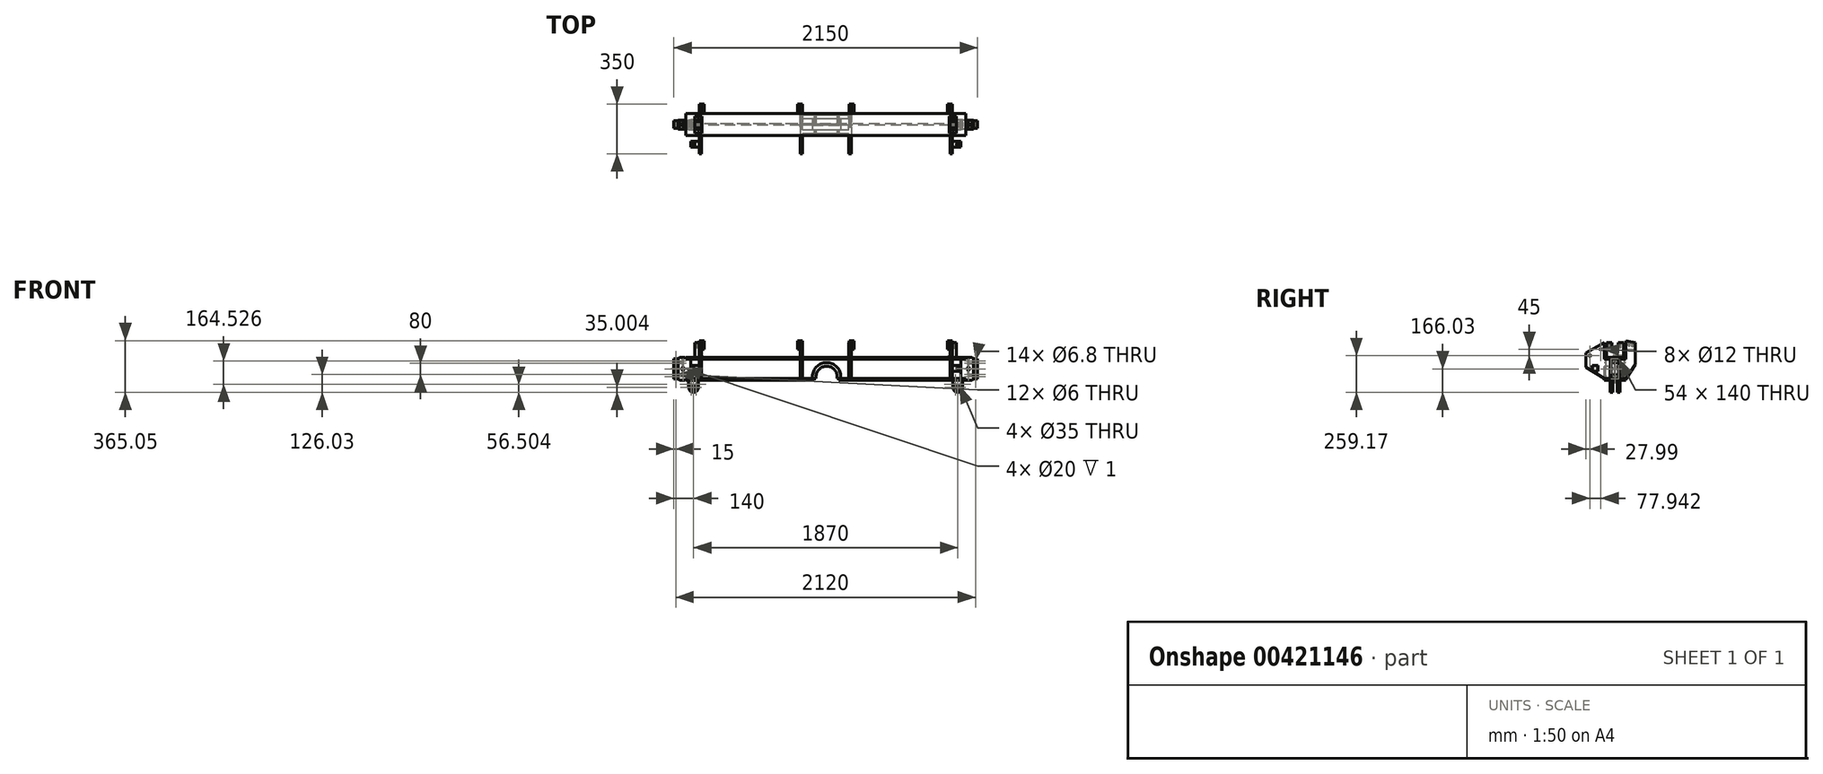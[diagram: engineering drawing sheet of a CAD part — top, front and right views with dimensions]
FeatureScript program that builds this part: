
annotation { "Feature Type Name" : "Feature", "Feature Type Description" : "" }
export const myFeature = defineFeature(function(context is Context, id is Id, definition is map)
    precondition{}
    {
        {
            var Q0;
            Q0=qCreatedBy(makeId("Right.planeOp"),FACE);
            var sketch = newSketch(context, id + "F0", { "sketchPlane" : qUnion([Q0])});
            skLineSegment(sketch, "E0.bottom", {"start": v(-77.22, 81.03) * mm, "end": v(77.22, 81.03) * mm});
            skLineSegment(sketch, "E0.top", {"start": v(-77.22, -81.03) * mm, "end": v(77.22, -81.03) * mm});
            skLineSegment(sketch, "E0.left", {"start": v(-77.22, 81.03) * mm, "end": v(-77.22, 69.47) * mm});
            skLineSegment(sketch, "E0.right", {"start": v(77.22, 81.03) * mm, "end": v(77.22, 69.47) * mm});
            skPoint(sketch, "E0.middle", {"position": v(0, 0) * mm});
            skLineSegment(sketch, "E1", {"start": v(0, 87.3) * mm, "end": v(0, -92.44) * mm, "construction": true});
            skLineSegment(sketch, "E2.0", {"start": v(-77.22, 69.47) * mm, "end": v(-16.76, 69.47) * mm});
            skLineSegment(sketch, "E3.0", {"start": v(-77.22, -69.47) * mm, "end": v(-16.76, -69.47) * mm});
            skLineSegment(sketch, "E4.0", {"start": v(-4.06, 56.77) * mm, "end": v(-4.06, -56.77) * mm});
            skLineSegment(sketch, "E5.0", {"start": v(4.06, 56.77) * mm, "end": v(4.06, -56.77) * mm});
            skLineSegment(sketch, "E6.trimOffspring", {"start": v(16.76, -69.47) * mm, "end": v(77.22, -69.47) * mm});
            skLineSegment(sketch, "E7.trimOffspring", {"start": v(16.76, 69.47) * mm, "end": v(77.22, 69.47) * mm});
            skLineSegment(sketch, "E8.trimOffspring", {"start": v(-77.22, -69.47) * mm, "end": v(-77.22, -81.03) * mm});
            skLineSegment(sketch, "E9.trimOffspring", {"start": v(77.22, -69.47) * mm, "end": v(77.22, -81.03) * mm});
            skPoint(sketch, "E10.visualSharp", {"position": v(-4.06, 69.47) * mm});
            skArc(sketch, "E10.filletArc", {"start": v(-4.06, 56.77) * mm, "mid": v(-7.78, 65.75) * mm, "end": v(-16.76, 69.47) * mm});
            skPoint(sketch, "E11.visualSharp", {"position": v(4.06, 69.47) * mm});
            skArc(sketch, "E11.filletArc", {"start": v(16.76, 69.47) * mm, "mid": v(7.78, 65.75) * mm, "end": v(4.06, 56.77) * mm});
            skPoint(sketch, "E12.visualSharp", {"position": v(4.06, -69.47) * mm});
            skArc(sketch, "E12.filletArc", {"start": v(4.06, -56.77) * mm, "mid": v(7.78, -65.75) * mm, "end": v(16.76, -69.47) * mm});
            skPoint(sketch, "E13.visualSharp", {"position": v(-4.06, -69.47) * mm});
            skArc(sketch, "E13.filletArc", {"start": v(-16.76, -69.47) * mm, "mid": v(-7.78, -65.75) * mm, "end": v(-4.06, -56.77) * mm});
            skSolve(sketch);
        }
        {
            var Q0;
            Q0=qSketchRegion(id+"F0",true);
            extrude(context, id + "F1", {"entities" : qUnion([Q0]), "endBound" : BoundingType.SYMMETRIC, "depth" : 1980 * mm});
        }
        {
            var Q0;
            Q0=makeQuery(id+"F1.opExtrude","SWEPT_FACE",FACE,{"disambiguationData":[OSD([sQuery(id+"F0.wireOp",EDGE,"E4.0")])]});
            var sketch = newSketch(context, id + "F2", { "sketchPlane" : qUnion([Q0])});
            skLineSegment(sketch, "E14", {"start": v(0, 173.84) * mm, "end": v(0, -192.2) * mm, "construction": true});
            skLineSegment(sketch, "E15.0", {"start": v(-990, 69.47) * mm, "end": v(-990, -69.47) * mm, "construction": true});
            skLineSegment(sketch, "E16.0", {"start": v(990, 69.47) * mm, "end": v(-990, 69.47) * mm, "construction": true});
            skLineSegment(sketch, "E17.0", {"start": v(990, -69.47) * mm, "end": v(-990, -69.47) * mm, "construction": true});
            skPoint(sketch, "E18.orphan", {"position": v(-990, 56.77) * mm});
            skPoint(sketch, "E19.orphan", {"position": v(-990, -56.77) * mm});
            skLineSegment(sketch, "E20.bottom", {"start": v(-990, 69.47) * mm, "end": v(-955, 69.47) * mm});
            skLineSegment(sketch, "E20.top", {"start": v(-990, -69.47) * mm, "end": v(-955, -69.47) * mm});
            skLineSegment(sketch, "E20.left", {"start": v(-990, 69.47) * mm, "end": v(-990, -69.47) * mm});
            skLineSegment(sketch, "E20.right", {"start": v(-955, 69.47) * mm, "end": v(-955, -69.47) * mm});
            skLineSegment(sketch, "E21.MirrorCS", {"start": v(990, -69.47) * mm, "end": v(955, -69.47) * mm});
            skLineSegment(sketch, "E22.MirrorCS", {"start": v(990, 69.47) * mm, "end": v(955, 69.47) * mm});
            skLineSegment(sketch, "E23.MirrorCS", {"start": v(990, 69.47) * mm, "end": v(990, -69.47) * mm});
            skLineSegment(sketch, "E24.MirrorCS", {"start": v(955, 69.47) * mm, "end": v(955, -69.47) * mm});
            skPoint(sketch, "E25.MirrorP", {"position": v(990, -56.77) * mm});
            skPoint(sketch, "E26.MirrorP", {"position": v(990, 56.77) * mm});
            skLineSegment(sketch, "E27.MirrorCS", {"start": v(990, 69.47) * mm, "end": v(990, -69.47) * mm, "construction": true});
            skSolve(sketch);
        }
        {
            var Q0;
            Q0=qSketchRegion(id+"F2",true);
            extrude(context, id + "F3", {"entities" : qUnion([Q0]), "operationType" : NewBodyOperationType.REMOVE, "endBound" : BoundingType.SYMMETRIC, "oppositeDirection" : true, "depth" : 50 * mm});
        }
        {
            var Q0;
            Q0=qCreatedBy(makeId("Front.planeOp"),FACE);
            var sketch = newSketch(context, id + "F4", { "sketchPlane" : qUnion([Q0])});
            skLineSegment(sketch, "E28", {"start": v(0, 276.7) * mm, "end": v(0, -349.05) * mm, "construction": true});
            skLineSegment(sketch, "E29.0", {"start": v(-1075, 276.7) * mm, "end": v(-1075, -349.05) * mm, "construction": true});
            skLineSegment(sketch, "E30.0", {"start": v(990, 81.03) * mm, "end": v(-1045, 81.03) * mm, "construction": true});
            skLineSegment(sketch, "E31.0", {"start": v(990, -81.03) * mm, "end": v(-1045, -81.03) * mm, "construction": true});
            skLineSegment(sketch, "E32.0", {"start": v(-955, -69.47) * mm, "end": v(-955, 69.47) * mm, "construction": true});
            skLineSegment(sketch, "E33.0", {"start": v(990, -69.47) * mm, "end": v(-990, -69.47) * mm, "construction": true});
            skLineSegment(sketch, "E34.0", {"start": v(990, 69.47) * mm, "end": v(-990, 69.47) * mm, "construction": true});
            skPoint(sketch, "E35.orphan", {"position": v(-955, 56.77) * mm});
            skPoint(sketch, "E36.orphan", {"position": v(-955, -56.77) * mm});
            skPoint(sketch, "E37.orphan", {"position": v(-990, 81.03) * mm});
            skPoint(sketch, "E38.orphan", {"position": v(-990, -81.03) * mm});
            skLineSegment(sketch, "E39", {"start": v(-990, 81.03) * mm, "end": v(-990, 69.47) * mm, "construction": true});
            skLineSegment(sketch, "E40.0", {"start": v(-1045, 81.03) * mm, "end": v(-1045, 70) * mm, "construction": true});
            skLineSegment(sketch, "E41", {"start": v(0, 0) * mm, "end": v(-1199.42, 0) * mm, "construction": true});
            skLineSegment(sketch, "E42.0", {"start": v(0, 70) * mm, "end": v(-990, 70) * mm, "construction": true});
            skLineSegment(sketch, "E43.trimOffspring", {"start": v(-1045, 70) * mm, "end": v(-1075, 70) * mm, "construction": true});
            skLineSegment(sketch, "E44.MirrorCS", {"start": v(-1045, -70) * mm, "end": v(-1075, -70) * mm, "construction": true});
            skPoint(sketch, "E45.orphan", {"position": v(-1199.42, 70) * mm});
            skPoint(sketch, "E46.orphan", {"position": v(-1199.42, -70) * mm});
            skLineSegment(sketch, "E47.trimOffspring", {"start": v(-1045, -70) * mm, "end": v(-1045, -81.03) * mm, "construction": true});
            skLineSegment(sketch, "E48.trimOffspring", {"start": v(-990, -69.47) * mm, "end": v(-990, -81.03) * mm, "construction": true});
            skLineSegment(sketch, "E49.bottom", {"start": v(-1075, 70) * mm, "end": v(-1045, 70) * mm});
            skLineSegment(sketch, "E49.top", {"start": v(-1075, -70) * mm, "end": v(-1045, -70) * mm});
            skLineSegment(sketch, "E49.left", {"start": v(-1075, 70) * mm, "end": v(-1075, -70) * mm});
            skLineSegment(sketch, "E50.bottom", {"start": v(-1045, 81.03) * mm, "end": v(-990, 81.03) * mm});
            skLineSegment(sketch, "E50.top", {"start": v(-1045, -81.03) * mm, "end": v(-990, -81.03) * mm});
            skLineSegment(sketch, "E50.left", {"start": v(-1045, 81.03) * mm, "end": v(-1045, 70) * mm});
            skLineSegment(sketch, "E50.right", {"start": v(-990, 81.03) * mm, "end": v(-990, 69.47) * mm});
            skLineSegment(sketch, "E51.bottom", {"start": v(-990, 70) * mm, "end": v(-955, 70) * mm});
            skLineSegment(sketch, "E51.top", {"start": v(-990, -69.47) * mm, "end": v(-955, -69.47) * mm});
            skLineSegment(sketch, "E51.left", {"start": v(-990, 70) * mm, "end": v(-990, 69.47) * mm});
            skLineSegment(sketch, "E51.right", {"start": v(-955, 70) * mm, "end": v(-955, -69.47) * mm});
            skLineSegment(sketch, "E52.trimOffspring", {"start": v(-990, -69.47) * mm, "end": v(-990, -81.03) * mm});
            skLineSegment(sketch, "E53.trimOffspring", {"start": v(-1045, -70) * mm, "end": v(-1045, -81.03) * mm});
            skSolve(sketch);
        }
        {
            var Q0;
            Q0=qSketchRegion(id+"F4",true);
            extrude(context, id + "F5", {"entities" : qUnion([Q0]), "endBound" : BoundingType.SYMMETRIC, "depth" : 63.5 * mm});
        }
        {
            var Q0;
            Q0=makeQuery(id+"F5.opExtrude","SWEPT_FACE",FACE,{"disambiguationData":[OSD([sQuery(id+"F4.wireOp",EDGE,"E49.bottom")])]});
            var sketch = newSketch(context, id + "F6", { "sketchPlane" : qUnion([Q0])});
            skLineSegment(sketch, "E54", {"start": v(-948.4, 0) * mm, "end": v(-1101.52, 0) * mm, "construction": true});
            skLineSegment(sketch, "E55.0", {"start": v(-1045, -31.75) * mm, "end": v(-1045, 31.75) * mm, "construction": true});
            skLineSegment(sketch, "E56.0", {"start": v(-948.4, 27) * mm, "end": v(-1101.52, 27) * mm, "construction": true});
            skLineSegment(sketch, "E57.bottom", {"start": v(-1075, 31.75) * mm, "end": v(-1045, 31.75) * mm});
            skLineSegment(sketch, "E57.top", {"start": v(-1075, 27) * mm, "end": v(-1045, 27) * mm});
            skLineSegment(sketch, "E57.left", {"start": v(-1075, 31.75) * mm, "end": v(-1075, 27) * mm});
            skLineSegment(sketch, "E57.right", {"start": v(-1045, 31.75) * mm, "end": v(-1045, 27) * mm});
            skLineSegment(sketch, "E58.MirrorCS", {"start": v(-1045, -31.75) * mm, "end": v(-1045, -27) * mm});
            skLineSegment(sketch, "E59.MirrorCS", {"start": v(-1075, -31.75) * mm, "end": v(-1075, -27) * mm});
            skLineSegment(sketch, "E60.MirrorCS", {"start": v(-1075, -27) * mm, "end": v(-1045, -27) * mm});
            skLineSegment(sketch, "E61.MirrorCS", {"start": v(-1075, -31.75) * mm, "end": v(-1045, -31.75) * mm});
            skSolve(sketch);
        }
        {
            var Q0;
            Q0=qSketchRegion(id+"F6",true);
            extrude(context, id + "F7", {"entities" : qUnion([Q0]), "operationType" : NewBodyOperationType.REMOVE, "endBound" : BoundingType.THROUGH_ALL, "oppositeDirection" : true, "depth" : 25 * mm});
        }
        {
            var Q0;
            Q0=makeQuery(id+"F5.opExtrude","SWEPT_FACE",FACE,{"disambiguationData":[OSD([sQuery(id+"F4.wireOp",EDGE,"E50.bottom")])]});
            var sketch = newSketch(context, id + "F8", { "sketchPlane" : qUnion([Q0])});
            skLineSegment(sketch, "E62.0", {"start": v(-1075, -27) * mm, "end": v(-1075, 27) * mm, "construction": true});
            skLineSegment(sketch, "E63", {"start": v(-919.6, 0) * mm, "end": v(-1088.25, 0) * mm, "construction": true});
            skPoint(sketch, "E63.endSnap0", {"position": v(-1075, 0) * mm});
            skLineSegment(sketch, "E64.0", {"start": v(-1010, -27) * mm, "end": v(-1010, 27) * mm, "construction": true});
            skPoint(sketch, "E65", {"position": v(-1010, 0) * mm});
            skSolve(sketch);
        }
        {
            var Q0;
            Q0=sQuery(id+"F8.wireOp",VERTEX,"E65");
            var Q1;
            Q1=makeQuery(id+"F5.opExtrude","SWEPT_BODY",BODY,{"disambiguationData":[OSD([sQuery(id+"F4.wireOp",EDGE,"E49.bottom"),sQuery(id+"F4.wireOp",EDGE,"E49.top"),sQuery(id+"F4.wireOp",EDGE,"E49.left"),sQuery(id+"F4.wireOp",EDGE,"E50.bottom"),sQuery(id+"F4.wireOp",EDGE,"E50.top"),sQuery(id+"F4.wireOp",EDGE,"E50.left"),sQuery(id+"F4.wireOp",EDGE,"E50.right"),sQuery(id+"F4.wireOp",EDGE,"E51.bottom"),sQuery(id+"F4.wireOp",EDGE,"E51.top"),sQuery(id+"F4.wireOp",EDGE,"E51.right"),sQuery(id+"F4.wireOp",EDGE,"E52.trimOffspring"),sQuery(id+"F4.wireOp",EDGE,"E53.trimOffspring")])]});
            hole(context, id + "F9", {"style" : HoleStyle.SIMPLE, "endStyle" : HoleEndStyle.BLIND, "standardTappedOrClearance" : lookupTablePath({ "standard" : "ISO", "size" : "6", "type" : "Drilled" }), "standardBlindInLast" : lookupTablePath({ "standard" : "ISO", "size" : "6", "type" : "Drilled" }), "holeDiameter" : 6 * mm, "holeDepth" : 125 * mm, "locations" : qUnion([Q0]), "scope" : qUnion([Q1])});
        }
        {
            var Q0;
            Q0=sQuery(id+"F8.wireOp",VERTEX,"E65");
            var Q1;
            Q1=makeQuery(id+"F5.opExtrude","SWEPT_BODY",BODY,{"disambiguationData":[OSD([sQuery(id+"F4.wireOp",EDGE,"E49.bottom"),sQuery(id+"F4.wireOp",EDGE,"E49.top"),sQuery(id+"F4.wireOp",EDGE,"E49.left"),sQuery(id+"F4.wireOp",EDGE,"E50.bottom"),sQuery(id+"F4.wireOp",EDGE,"E50.top"),sQuery(id+"F4.wireOp",EDGE,"E50.left"),sQuery(id+"F4.wireOp",EDGE,"E50.right"),sQuery(id+"F4.wireOp",EDGE,"E51.bottom"),sQuery(id+"F4.wireOp",EDGE,"E51.top"),sQuery(id+"F4.wireOp",EDGE,"E51.right"),sQuery(id+"F4.wireOp",EDGE,"E52.trimOffspring"),sQuery(id+"F4.wireOp",EDGE,"E53.trimOffspring")])]});
            hole(context, id + "F10", {"style" : HoleStyle.SIMPLE, "endStyle" : HoleEndStyle.BLIND, "standardTappedOrClearance" : lookupTablePath({ "standard" : "ANSI", "engagement" : "75%", "pitch" : "13 tpi", "size" : "1/2", "type" : "Tapped" }), "standardBlindInLast" : lookupTablePath({ "standard" : "ANSI", "engagement" : "75%", "pitch" : "13 tpi", "size" : "1/2", "type" : "Tapped" }), "holeDiameter" : 10.72 * mm, "holeDepth" : 15 * mm, "locations" : qUnion([Q0]), "scope" : qUnion([Q1]), "majorDiameter" : 12.7 * mm});
        }
        {
            var Q0;
            {var subQ0=sQuery(id+"F4.wireOp",EDGE,"E50.bottom");Q0=makeQuery(id+"F8.imprint","IMPRINT",FACE,{"disambiguationData":[TD([[makeQuery(id+"F8.imprint","IMPRINT",EDGE,{"derivedFrom":makeQuery(id+"F5.opExtrude","CAP_EDGE",EDGE,{"disambiguationData":[OSD([subQ0])],"isStart":true})}),-1.0]])]});}
            var sketch = newSketch(context, id + "F11", { "sketchPlane" : qUnion([Q0])});
            skPoint(sketch, "E66.0", {"position": v(-1010, 0) * mm});
            skCircle(sketch, "E67", {"center": v(-1010, 0) * mm, "radius": 10 * mm});
            skSolve(sketch);
        }
        {
            var Q0;
            Q0=qSketchRegion(id+"F11",true);
            extrude(context, id + "F12", {"entities" : qUnion([Q0]), "operationType" : NewBodyOperationType.REMOVE, "oppositeDirection" : true, "depth" : 1 * mm});
        }
        {
            var Q0;
            Q0=makeQuery(id+"F5.opExtrude","SWEPT_EDGE",EDGE,{"disambiguationData":[OSD([sQuery(id+"F4.wireOp",EDGE,"E50.bottom"),sQuery(id+"F4.wireOp",EDGE,"E50.left")])]});
            var Q1;
            Q1=makeQuery(id+"F7.boolean.opBoolean","INTERSECT",EDGE,{"derivedFrom":[makeQuery(id+"F7.opExtrude","SWEPT_FACE",FACE,{"disambiguationData":[OSD([sQuery(id+"F6.wireOp",EDGE,"E57.right")])]}),makeQuery(id+"F7.opExtrude","SWEPT_FACE",FACE,{"disambiguationData":[OSD([sQuery(id+"F6.wireOp",EDGE,"E58.MirrorCS")])]})]});
            chamfer(context, id + "F13", {"entities" : qUnion([Q0, Q1]), "width" : 11 * mm, "tangentPropagation" : true});
        }
        {
            var Q0;
            Q0=makeQuery(id+"F5.opExtrude","CAP_FACE",FACE,{"disambiguationData":[OSD([sQuery(id+"F4.wireOp",EDGE,"E49.bottom"),sQuery(id+"F4.wireOp",EDGE,"E49.top"),sQuery(id+"F4.wireOp",EDGE,"E49.left"),sQuery(id+"F4.wireOp",EDGE,"E50.bottom"),sQuery(id+"F4.wireOp",EDGE,"E50.top"),sQuery(id+"F4.wireOp",EDGE,"E50.left"),sQuery(id+"F4.wireOp",EDGE,"E50.right"),sQuery(id+"F4.wireOp",EDGE,"E51.bottom"),sQuery(id+"F4.wireOp",EDGE,"E51.top"),sQuery(id+"F4.wireOp",EDGE,"E51.right"),sQuery(id+"F4.wireOp",EDGE,"E52.trimOffspring"),sQuery(id+"F4.wireOp",EDGE,"E53.trimOffspring")])],"isStart":false});
            var sketch = newSketch(context, id + "F14", { "sketchPlane" : qUnion([Q0])});
            skLineSegment(sketch, "E68", {"start": v(-947.26, 0.27) * mm, "end": v(-1104.17, 0.27) * mm, "construction": true});
            skPoint(sketch, "E68.startSnap0", {"position": v(-955, 0.27) * mm});
            skLineSegment(sketch, "E69.0", {"start": v(-1075, -70) * mm, "end": v(-1075, 70) * mm, "construction": true});
            skLineSegment(sketch, "E70.0", {"start": v(-1010, -70) * mm, "end": v(-1010, 70) * mm, "construction": true});
            skPoint(sketch, "E71", {"position": v(-1010, 0.27) * mm});
            skSolve(sketch);
        }
        {
            var Q0;
            Q0=sQuery(id+"F14.wireOp",VERTEX,"E71");
            var Q1;
            Q1=makeQuery(id+"F5.opExtrude","SWEPT_BODY",BODY,{"disambiguationData":[OSD([sQuery(id+"F4.wireOp",EDGE,"E49.bottom"),sQuery(id+"F4.wireOp",EDGE,"E49.top"),sQuery(id+"F4.wireOp",EDGE,"E49.left"),sQuery(id+"F4.wireOp",EDGE,"E50.bottom"),sQuery(id+"F4.wireOp",EDGE,"E50.top"),sQuery(id+"F4.wireOp",EDGE,"E50.left"),sQuery(id+"F4.wireOp",EDGE,"E50.right"),sQuery(id+"F4.wireOp",EDGE,"E51.bottom"),sQuery(id+"F4.wireOp",EDGE,"E51.top"),sQuery(id+"F4.wireOp",EDGE,"E51.right"),sQuery(id+"F4.wireOp",EDGE,"E52.trimOffspring"),sQuery(id+"F4.wireOp",EDGE,"E53.trimOffspring")])]});
            hole(context, id + "F15", {"style" : HoleStyle.SIMPLE, "endStyle" : HoleEndStyle.BLIND, "standardTappedOrClearance" : lookupTablePath({ "standard" : "ANSI", "engagement" : "75%", "pitch" : "13 tpi", "size" : "1/2", "type" : "Tapped" }), "standardBlindInLast" : lookupTablePath({ "standard" : "ANSI", "engagement" : "75%", "pitch" : "13 tpi", "size" : "1/2", "type" : "Tapped" }), "holeDiameter" : 10.72 * mm, "holeDepth" : 15 * mm, "locations" : qUnion([Q0]), "scope" : qUnion([Q1]), "majorDiameter" : 12.7 * mm});
        }
        {
            var Q0;
            Q0=sQuery(id+"F14.wireOp",VERTEX,"E71");
            var Q1;
            Q1=makeQuery(id+"F5.opExtrude","SWEPT_BODY",BODY,{"disambiguationData":[OSD([sQuery(id+"F4.wireOp",EDGE,"E49.bottom"),sQuery(id+"F4.wireOp",EDGE,"E49.top"),sQuery(id+"F4.wireOp",EDGE,"E49.left"),sQuery(id+"F4.wireOp",EDGE,"E50.bottom"),sQuery(id+"F4.wireOp",EDGE,"E50.top"),sQuery(id+"F4.wireOp",EDGE,"E50.left"),sQuery(id+"F4.wireOp",EDGE,"E50.right"),sQuery(id+"F4.wireOp",EDGE,"E51.bottom"),sQuery(id+"F4.wireOp",EDGE,"E51.top"),sQuery(id+"F4.wireOp",EDGE,"E51.right"),sQuery(id+"F4.wireOp",EDGE,"E52.trimOffspring"),sQuery(id+"F4.wireOp",EDGE,"E53.trimOffspring")])]});
            hole(context, id + "F16", {"style" : HoleStyle.SIMPLE, "endStyle" : HoleEndStyle.THROUGH, "standardTappedOrClearance" : lookupTablePath({ "standard" : "ISO", "size" : "6", "type" : "Drilled" }), "standardBlindInLast" : lookupTablePath({ "standard" : "ISO", "size" : "6", "type" : "Drilled" }), "holeDiameter" : 6 * mm, "locations" : qUnion([Q0]), "scope" : qUnion([Q1]), "isTappedThrough" : true});
        }
        {
            var Q0;
            {var subQ4=sQuery(id+"F4.wireOp",EDGE,"E50.right");Q0=makeQuery(id+"F14.imprint","IMPRINT",FACE,{"disambiguationData":[TD([[makeQuery(id+"F14.imprint","IMPRINT",EDGE,{"derivedFrom":makeQuery(id+"F5.opExtrude","CAP_EDGE",EDGE,{"disambiguationData":[OSD([subQ4])],"isStart":false})}),-1.0]])]});}
            var sketch = newSketch(context, id + "F17", { "sketchPlane" : qUnion([Q0])});
            skCircle(sketch, "E72", {"center": v(-1010, 0.27) * mm, "radius": 10 * mm});
            skSolve(sketch);
        }
        {
            var Q0;
            Q0=qSketchRegion(id+"F17",true);
            extrude(context, id + "F18", {"entities" : qUnion([Q0]), "operationType" : NewBodyOperationType.REMOVE, "oppositeDirection" : true, "depth" : 1 * mm});
        }
        {
            var Q0;
            Q0=makeQuery(id+"F5.opExtrude","CAP_FACE",FACE,{"disambiguationData":[OSD([sQuery(id+"F4.wireOp",EDGE,"E49.bottom"),sQuery(id+"F4.wireOp",EDGE,"E49.top"),sQuery(id+"F4.wireOp",EDGE,"E49.left"),sQuery(id+"F4.wireOp",EDGE,"E50.bottom"),sQuery(id+"F4.wireOp",EDGE,"E50.top"),sQuery(id+"F4.wireOp",EDGE,"E50.left"),sQuery(id+"F4.wireOp",EDGE,"E50.right"),sQuery(id+"F4.wireOp",EDGE,"E51.bottom"),sQuery(id+"F4.wireOp",EDGE,"E51.top"),sQuery(id+"F4.wireOp",EDGE,"E51.right"),sQuery(id+"F4.wireOp",EDGE,"E52.trimOffspring"),sQuery(id+"F4.wireOp",EDGE,"E53.trimOffspring")])],"isStart":true});
            var sketch = newSketch(context, id + "F19", { "sketchPlane" : qUnion([Q0])});
            skCircle(sketch, "E73.0", {"center": v(1010, 0.27) * mm, "radius": 10 * mm, "construction": true});
            skCircle(sketch, "E74", {"center": v(1010, 0.27) * mm, "radius": 10 * mm});
            skSolve(sketch);
        }
        {
            var Q0;
            Q0=qSketchRegion(id+"F19",true);
            extrude(context, id + "F20", {"entities" : qUnion([Q0]), "operationType" : NewBodyOperationType.REMOVE, "oppositeDirection" : true, "depth" : 1 * mm});
        }
        {
            var Q0;
            Q0=sQuery(id+"F19.wireOp",VERTEX,"E73.0.center");
            var Q1;
            Q1=makeQuery(id+"F5.opExtrude","SWEPT_BODY",BODY,{"disambiguationData":[OSD([sQuery(id+"F4.wireOp",EDGE,"E49.bottom"),sQuery(id+"F4.wireOp",EDGE,"E49.top"),sQuery(id+"F4.wireOp",EDGE,"E49.left"),sQuery(id+"F4.wireOp",EDGE,"E50.bottom"),sQuery(id+"F4.wireOp",EDGE,"E50.top"),sQuery(id+"F4.wireOp",EDGE,"E50.left"),sQuery(id+"F4.wireOp",EDGE,"E50.right"),sQuery(id+"F4.wireOp",EDGE,"E51.bottom"),sQuery(id+"F4.wireOp",EDGE,"E51.top"),sQuery(id+"F4.wireOp",EDGE,"E51.right"),sQuery(id+"F4.wireOp",EDGE,"E52.trimOffspring"),sQuery(id+"F4.wireOp",EDGE,"E53.trimOffspring")])]});
            hole(context, id + "F21", {"style" : HoleStyle.SIMPLE, "endStyle" : HoleEndStyle.BLIND, "standardTappedOrClearance" : lookupTablePath({ "standard" : "ANSI", "engagement" : "75%", "pitch" : "13 tpi", "size" : "1/2", "type" : "Tapped" }), "standardBlindInLast" : lookupTablePath({ "standard" : "ANSI", "engagement" : "75%", "pitch" : "13 tpi", "size" : "1/2", "type" : "Tapped" }), "holeDiameter" : 10.72 * mm, "holeDepth" : 15 * mm, "locations" : qUnion([Q0]), "scope" : qUnion([Q1]), "majorDiameter" : 12.7 * mm});
        }
        {
            var Q0;
            Q0=makeQuery(id+"F7.boolean.opBoolean","COPY",FACE,{"derivedFrom":makeQuery(id+"F7.opExtrude","SWEPT_FACE",FACE,{"disambiguationData":[OSD([sQuery(id+"F6.wireOp",EDGE,"E60.MirrorCS")])]})});
            var sketch = newSketch(context, id + "F22", { "sketchPlane" : qUnion([Q0])});
            skLineSegment(sketch, "E75.0", {"start": v(-1075, -70) * mm, "end": v(-1075, 70) * mm, "construction": true});
            skLineSegment(sketch, "E76.0", {"start": v(-1060, -70) * mm, "end": v(-1060, 70) * mm, "construction": true});
            skLineSegment(sketch, "E77", {"start": v(-1060, 0) * mm, "end": v(-1136.9, 0) * mm, "construction": true});
            skLineSegment(sketch, "E78.0", {"start": v(-1060, 55) * mm, "end": v(-1136.9, 55) * mm, "construction": true});
            skLineSegment(sketch, "E79.0", {"start": v(-1060, -55) * mm, "end": v(-1136.9, -55) * mm, "construction": true});
            skPoint(sketch, "E80", {"position": v(-1060, 55) * mm});
            skPoint(sketch, "E81", {"position": v(-1060, 0) * mm});
            skPoint(sketch, "E82", {"position": v(-1060, -55) * mm});
            skSolve(sketch);
        }
        {
            var Q0;
            Q0=sQuery(id+"F22.wireOp",VERTEX,"E80");
            var Q1;
            Q1=sQuery(id+"F22.wireOp",VERTEX,"E81");
            var Q2;
            Q2=sQuery(id+"F22.wireOp",VERTEX,"E82");
            var Q3;
            Q3=makeQuery(id+"F5.opExtrude","SWEPT_BODY",BODY,{"disambiguationData":[OSD([sQuery(id+"F4.wireOp",EDGE,"E49.bottom"),sQuery(id+"F4.wireOp",EDGE,"E49.top"),sQuery(id+"F4.wireOp",EDGE,"E49.left"),sQuery(id+"F4.wireOp",EDGE,"E50.bottom"),sQuery(id+"F4.wireOp",EDGE,"E50.top"),sQuery(id+"F4.wireOp",EDGE,"E50.left"),sQuery(id+"F4.wireOp",EDGE,"E50.right"),sQuery(id+"F4.wireOp",EDGE,"E51.bottom"),sQuery(id+"F4.wireOp",EDGE,"E51.top"),sQuery(id+"F4.wireOp",EDGE,"E51.right"),sQuery(id+"F4.wireOp",EDGE,"E52.trimOffspring"),sQuery(id+"F4.wireOp",EDGE,"E53.trimOffspring")])]});
            hole(context, id + "F23", {"style" : HoleStyle.SIMPLE, "endStyle" : HoleEndStyle.THROUGH, "standardTappedOrClearance" : lookupTablePath({ "standard" : "ISO", "engagement" : "75%", "pitch" : "1.25 mm", "size" : "M8", "type" : "Tapped" }), "standardBlindInLast" : lookupTablePath({ "standard" : "ISO", "engagement" : "75%", "pitch" : "1.25 mm", "size" : "M8", "type" : "Tapped" }), "holeDiameter" : 6.8 * mm, "locations" : qUnion([Q0, Q1, Q2]), "scope" : qUnion([Q3]), "isTappedThrough" : true, "majorDiameter" : 8 * mm, "showTappedDepth" : true});
        }
        {
            var Q0;
            Q0=makeQuery(id+"F7.boolean.opBoolean","COPY",FACE,{"derivedFrom":makeQuery(id+"F7.opExtrude","SWEPT_FACE",FACE,{"disambiguationData":[OSD([sQuery(id+"F6.wireOp",EDGE,"E60.MirrorCS")])]})});
            var sketch = newSketch(context, id + "F24", { "sketchPlane" : qUnion([Q0])});
            skLineSegment(sketch, "E83.0", {"start": v(-1060, 0) * mm, "end": v(-1136.9, 0) * mm, "construction": true});
            skLineSegment(sketch, "E84.0", {"start": v(-1060, -70) * mm, "end": v(-1060, 70) * mm, "construction": true});
            skLineSegment(sketch, "E85.0", {"start": v(-1060, 40) * mm, "end": v(-1136.9, 40) * mm, "construction": true});
            skPoint(sketch, "E86", {"position": v(-1060, 40) * mm});
            skPoint(sketch, "E87.MirrorP", {"position": v(-1060, -40) * mm});
            skSolve(sketch);
        }
        {
            var Q0;
            Q0=sQuery(id+"F24.wireOp",VERTEX,"E86");
            var Q1;
            Q1=sQuery(id+"F24.wireOp",VERTEX,"E87.MirrorP");
            var Q2;
            Q2=makeQuery(id+"F5.opExtrude","SWEPT_BODY",BODY,{"disambiguationData":[OSD([sQuery(id+"F4.wireOp",EDGE,"E49.bottom"),sQuery(id+"F4.wireOp",EDGE,"E49.top"),sQuery(id+"F4.wireOp",EDGE,"E49.left"),sQuery(id+"F4.wireOp",EDGE,"E50.bottom"),sQuery(id+"F4.wireOp",EDGE,"E50.top"),sQuery(id+"F4.wireOp",EDGE,"E50.left"),sQuery(id+"F4.wireOp",EDGE,"E50.right"),sQuery(id+"F4.wireOp",EDGE,"E51.bottom"),sQuery(id+"F4.wireOp",EDGE,"E51.top"),sQuery(id+"F4.wireOp",EDGE,"E51.right"),sQuery(id+"F4.wireOp",EDGE,"E52.trimOffspring"),sQuery(id+"F4.wireOp",EDGE,"E53.trimOffspring")])]});
            hole(context, id + "F25", {"style" : HoleStyle.SIMPLE, "endStyle" : HoleEndStyle.THROUGH, "standardTappedOrClearance" : lookupTablePath({ "standard" : "ISO", "size" : "6", "type" : "Drilled" }), "standardBlindInLast" : lookupTablePath({ "standard" : "ISO", "size" : "6", "type" : "Drilled" }), "holeDiameter" : 6 * mm, "locations" : qUnion([Q0, Q1]), "scope" : qUnion([Q2]), "isTappedThrough" : true});
        }
        {
            var Q0;
            Q0=makeQuery(id+"F5.opExtrude","SWEPT_FACE",FACE,{"disambiguationData":[OSD([sQuery(id+"F4.wireOp",EDGE,"E49.left")])]});
            var sketch = newSketch(context, id + "F26", { "sketchPlane" : qUnion([Q0])});
            skLineSegment(sketch, "E88.0.0", {"start": v(-27, -70) * mm, "end": v(27, -70) * mm, "construction": true});
            skLineSegment(sketch, "E88.0.1", {"start": v(27, -70) * mm, "end": v(27, 70) * mm, "construction": true});
            skLineSegment(sketch, "E88.0.2", {"start": v(27, 70) * mm, "end": v(-27, 70) * mm, "construction": true});
            skLineSegment(sketch, "E88.0.3", {"start": v(-27, 70) * mm, "end": v(-27, -70) * mm, "construction": true});
            skLineSegment(sketch, "E89", {"start": v(-27, 0) * mm, "end": v(56.48, 0) * mm, "construction": true});
            skPoint(sketch, "E89.endSnap0", {"position": v(-27, 0) * mm});
            skLineSegment(sketch, "E90", {"start": v(0, 96.87) * mm, "end": v(0, -94.28) * mm, "construction": true});
            skLineSegment(sketch, "E91.0", {"start": v(-27, -40) * mm, "end": v(56.48, -40) * mm, "construction": true});
            skPoint(sketch, "E92", {"position": v(0, -40) * mm});
            skPoint(sketch, "E93.MirrorP", {"position": v(0, 40) * mm});
            skSolve(sketch);
        }
        {
            var Q0;
            Q0=sQuery(id+"F26.wireOp",VERTEX,"E93.MirrorP");
            var Q1;
            Q1=sQuery(id+"F26.wireOp",VERTEX,"E92");
            var Q2;
            Q2=makeQuery(id+"F5.opExtrude","SWEPT_BODY",BODY,{"disambiguationData":[OSD([sQuery(id+"F4.wireOp",EDGE,"E49.bottom"),sQuery(id+"F4.wireOp",EDGE,"E49.top"),sQuery(id+"F4.wireOp",EDGE,"E49.left"),sQuery(id+"F4.wireOp",EDGE,"E50.bottom"),sQuery(id+"F4.wireOp",EDGE,"E50.top"),sQuery(id+"F4.wireOp",EDGE,"E50.left"),sQuery(id+"F4.wireOp",EDGE,"E50.right"),sQuery(id+"F4.wireOp",EDGE,"E51.bottom"),sQuery(id+"F4.wireOp",EDGE,"E51.top"),sQuery(id+"F4.wireOp",EDGE,"E51.right"),sQuery(id+"F4.wireOp",EDGE,"E52.trimOffspring"),sQuery(id+"F4.wireOp",EDGE,"E53.trimOffspring")])]});
            hole(context, id + "F27", {"style" : HoleStyle.SIMPLE, "endStyle" : HoleEndStyle.BLIND, "standardTappedOrClearance" : lookupTablePath({ "standard" : "ISO", "size" : "6", "type" : "Drilled" }), "standardBlindInLast" : lookupTablePath({ "standard" : "ISO", "size" : "6", "type" : "Drilled" }), "holeDiameter" : 6 * mm, "holeDepth" : 65 * mm, "locations" : qUnion([Q0, Q1]), "scope" : qUnion([Q2])});
        }
        {
            var Q0;
            Q0=sQuery(id+"F26.wireOp",VERTEX,"E93.MirrorP");
            var Q1;
            Q1=sQuery(id+"F26.wireOp",VERTEX,"E92");
            var Q2;
            Q2=makeQuery(id+"F5.opExtrude","SWEPT_BODY",BODY,{"disambiguationData":[OSD([sQuery(id+"F4.wireOp",EDGE,"E49.bottom"),sQuery(id+"F4.wireOp",EDGE,"E49.top"),sQuery(id+"F4.wireOp",EDGE,"E49.left"),sQuery(id+"F4.wireOp",EDGE,"E50.bottom"),sQuery(id+"F4.wireOp",EDGE,"E50.top"),sQuery(id+"F4.wireOp",EDGE,"E50.left"),sQuery(id+"F4.wireOp",EDGE,"E50.right"),sQuery(id+"F4.wireOp",EDGE,"E51.bottom"),sQuery(id+"F4.wireOp",EDGE,"E51.top"),sQuery(id+"F4.wireOp",EDGE,"E51.right"),sQuery(id+"F4.wireOp",EDGE,"E52.trimOffspring"),sQuery(id+"F4.wireOp",EDGE,"E53.trimOffspring")])]});
            hole(context, id + "F28", {"style" : HoleStyle.SIMPLE, "endStyle" : HoleEndStyle.BLIND, "standardTappedOrClearance" : lookupTablePath({ "standard" : "ISO", "engagement" : "75%", "pitch" : "1.25 mm", "size" : "M8", "type" : "Tapped" }), "standardBlindInLast" : lookupTablePath({ "standard" : "ISO", "engagement" : "75%", "pitch" : "1.25 mm", "size" : "M8", "type" : "Tapped" }), "holeDiameter" : 6.8 * mm, "holeDepth" : 12 * mm, "locations" : qUnion([Q0, Q1]), "scope" : qUnion([Q2]), "majorDiameter" : 8 * mm});
        }
        {
            var Q0;
            Q0=makeQuery(id+"F5.opExtrude","SWEPT_BODY",BODY,{"disambiguationData":[OSD([sQuery(id+"F4.wireOp",EDGE,"E49.bottom"),sQuery(id+"F4.wireOp",EDGE,"E49.top"),sQuery(id+"F4.wireOp",EDGE,"E49.left"),sQuery(id+"F4.wireOp",EDGE,"E50.bottom"),sQuery(id+"F4.wireOp",EDGE,"E50.top"),sQuery(id+"F4.wireOp",EDGE,"E50.left"),sQuery(id+"F4.wireOp",EDGE,"E50.right"),sQuery(id+"F4.wireOp",EDGE,"E51.bottom"),sQuery(id+"F4.wireOp",EDGE,"E51.top"),sQuery(id+"F4.wireOp",EDGE,"E51.right"),sQuery(id+"F4.wireOp",EDGE,"E52.trimOffspring"),sQuery(id+"F4.wireOp",EDGE,"E53.trimOffspring")])]});
            var Q1;
            Q1=qCreatedBy(makeId("Right.planeOp"),FACE);
            mirror(context, id + "F29", {"entities" : qUnion([Q0]), "mirrorPlane" : qUnion([Q1])});
        }
        {
            var Q0;
            Q0=qCreatedBy(makeId("Front.planeOp"),FACE);
            var sketch = newSketch(context, id + "F30", { "sketchPlane" : qUnion([Q0])});
            skLineSegment(sketch, "E94", {"start": v(0, 217.37) * mm, "end": v(0, -483.51) * mm, "construction": true});
            skLineSegment(sketch, "E95.0", {"start": v(-935, 217.37) * mm, "end": v(-935, -483.51) * mm, "construction": true});
            skLineSegment(sketch, "E96.0.0", {"start": v(-990, -69.47) * mm, "end": v(-990, -81.03) * mm, "construction": true});
            skLineSegment(sketch, "E96.0.1", {"start": v(-990, -81.03) * mm, "end": v(-900, -81.03) * mm});
            skLineSegment(sketch, "E96.0.2", {"start": v(990, -81.03) * mm, "end": v(990, -69.47) * mm, "construction": true});
            skLineSegment(sketch, "E96.0.3", {"start": v(990, -69.47) * mm, "end": v(-990, -69.47) * mm, "construction": true});
            skLineSegment(sketch, "E97.0", {"start": v(-990, -131.03) * mm, "end": v(990, -131.03) * mm, "construction": true});
            skCircle(sketch, "E98", {"center": v(-935, -131.03) * mm, "radius": 17.5 * mm});
            skArc(sketch, "E99", {"start": v(-970, -131.03) * mm, "mid": v(-935, -166.03) * mm, "end": v(-900, -131.03) * mm});
            skLineSegment(sketch, "E100", {"start": v(-970, -131.03) * mm, "end": v(-970, -81.03) * mm});
            skLineSegment(sketch, "E101", {"start": v(-900, -131.03) * mm, "end": v(-900, -81.03) * mm});
            skLineSegment(sketch, "E102.trimOffspring", {"start": v(0, -81.03) * mm, "end": v(990, -81.03) * mm});
            skLineSegment(sketch, "E103", {"start": v(-935, -166.03) * mm, "end": v(-989.6, -166.03) * mm, "construction": true});
            skLineSegment(sketch, "E104.0", {"start": v(-935, -144.53) * mm, "end": v(-989.6, -144.53) * mm, "construction": true});
            skLineSegment(sketch, "E105.0", {"start": v(-990, -109.53) * mm, "end": v(990, -109.53) * mm, "construction": true});
            skLineSegment(sketch, "E106.0", {"start": v(-953, 217.37) * mm, "end": v(-953, -483.51) * mm, "construction": true});
            skPoint(sketch, "E107", {"position": v(-953, -109.53) * mm});
            skPoint(sketch, "E108.MirrorP", {"position": v(-917, -109.53) * mm});
            skSolve(sketch);
        }
        {
            var Q0;
            Q0=qSketchRegion(id+"F30",true);
            extrude(context, id + "F31", {"entities" : qUnion([Q0]), "endBound" : BoundingType.SYMMETRIC, "depth" : 70 * mm});
        }
        {
            var Q0;
            Q0=makeQuery(id+"F31.opExtrude","CAP_FACE",FACE,{"disambiguationData":[OSD([sQuery(id+"F30.wireOp",EDGE,"E96.0.1"),sQuery(id+"F30.wireOp",EDGE,"E98"),sQuery(id+"F30.wireOp",EDGE,"E99"),sQuery(id+"F30.wireOp",EDGE,"E100"),sQuery(id+"F30.wireOp",EDGE,"E101")])],"isStart":false});
            var sketch = newSketch(context, id + "F32", { "sketchPlane" : qUnion([Q0])});
            skPoint(sketch, "E109.0", {"position": v(-953, -109.53) * mm});
            skPoint(sketch, "E110.0", {"position": v(-917, -109.53) * mm});
            skSolve(sketch);
        }
        {
            var Q0;
            Q0=sQuery(id+"F32.wireOp",VERTEX,"E109.0");
            var Q1;
            Q1=sQuery(id+"F32.wireOp",VERTEX,"E110.0");
            var Q2;
            Q2=makeQuery(id+"F31.opExtrude","SWEPT_BODY",BODY,{"disambiguationData":[OSD([sQuery(id+"F30.wireOp",EDGE,"E96.0.1"),sQuery(id+"F30.wireOp",EDGE,"E98"),sQuery(id+"F30.wireOp",EDGE,"E99"),sQuery(id+"F30.wireOp",EDGE,"E100"),sQuery(id+"F30.wireOp",EDGE,"E101")])]});
            hole(context, id + "F33", {"style" : HoleStyle.SIMPLE, "endStyle" : HoleEndStyle.THROUGH, "standardTappedOrClearance" : lookupTablePath({ "standard" : "ISO", "engagement" : "75%", "pitch" : "1.25 mm", "size" : "M8", "type" : "Tapped" }), "standardBlindInLast" : lookupTablePath({ "standard" : "ISO", "engagement" : "75%", "pitch" : "1.25 mm", "size" : "M8", "type" : "Tapped" }), "holeDiameter" : 6.8 * mm, "locations" : qUnion([Q0, Q1]), "scope" : qUnion([Q2]), "isTappedThrough" : true, "majorDiameter" : 8 * mm, "showTappedDepth" : true});
        }
        {
            var Q0;
            Q0=makeQuery(id+"F31.opExtrude","SWEPT_FACE",FACE,{"disambiguationData":[OSD([sQuery(id+"F30.wireOp",EDGE,"E101")])]});
            var sketch = newSketch(context, id + "F34", { "sketchPlane" : qUnion([Q0])});
            skLineSegment(sketch, "E111.0", {"start": v(-35, -81.03) * mm, "end": v(35, -81.03) * mm, "construction": true});
            skLineSegment(sketch, "E112", {"start": v(0, -81.03) * mm, "end": v(0, -181.86) * mm, "construction": true});
            skPoint(sketch, "E112.endSnap0", {"position": v(0, -81.03) * mm});
            skLineSegment(sketch, "E113.0", {"start": v(-15.5, -81.03) * mm, "end": v(-15.5, -181.86) * mm, "construction": true});
            skLineSegment(sketch, "E114", {"start": v(35, -166.03) * mm, "end": v(-35, -166.03) * mm, "construction": true});
            skLineSegment(sketch, "E115.0", {"start": v(35, -148.53) * mm, "end": v(35, -113.53) * mm, "construction": true});
            skLineSegment(sketch, "E116", {"start": v(35, -131.03) * mm, "end": v(-53.23, -131.03) * mm, "construction": true});
            skLineSegment(sketch, "E117.0", {"start": v(35, -87.03) * mm, "end": v(-53.23, -87.03) * mm, "construction": true});
            skLineSegment(sketch, "E118.bottom", {"start": v(-15.5, -166.03) * mm, "end": v(15.5, -166.03) * mm});
            skLineSegment(sketch, "E118.top", {"start": v(-15.5, -87.03) * mm, "end": v(15.5, -87.03) * mm});
            skLineSegment(sketch, "E118.left", {"start": v(-15.5, -166.03) * mm, "end": v(-15.5, -87.03) * mm});
            skLineSegment(sketch, "E118.right", {"start": v(15.5, -166.03) * mm, "end": v(15.5, -87.03) * mm});
            skSolve(sketch);
        }
        {
            var Q0;
            Q0=qSketchRegion(id+"F34",true);
            extrude(context, id + "F35", {"entities" : qUnion([Q0]), "operationType" : NewBodyOperationType.REMOVE, "endBound" : BoundingType.THROUGH_ALL, "oppositeDirection" : true, "depth" : 25 * mm});
        }
        {
            var Q0;
            Q0=makeQuery(id+"F35.boolean.opBoolean","COPY",EDGE,{"derivedFrom":makeQuery(id+"F35.opExtrude","SWEPT_EDGE",EDGE,{"disambiguationData":[OSD([sQuery(id+"F34.wireOp",EDGE,"E118.top"),sQuery(id+"F34.wireOp",EDGE,"E118.right")])]})});
            var Q1;
            Q1=makeQuery(id+"F35.boolean.opBoolean","COPY",EDGE,{"derivedFrom":makeQuery(id+"F35.opExtrude","SWEPT_EDGE",EDGE,{"disambiguationData":[OSD([sQuery(id+"F34.wireOp",EDGE,"E118.top"),sQuery(id+"F34.wireOp",EDGE,"E118.left")])]})});
            fillet(context, id + "F36", {"entities" : qUnion([Q0, Q1]), "radius" : 2 * mm, "tangentPropagation" : true, "allowEdgeOverflow" : false});
        }
        {
            var Q0;
            Q0=makeQuery(id+"F31.opExtrude","SWEPT_BODY",BODY,{"disambiguationData":[OSD([sQuery(id+"F30.wireOp",EDGE,"E96.0.1"),sQuery(id+"F30.wireOp",EDGE,"E98"),sQuery(id+"F30.wireOp",EDGE,"E99"),sQuery(id+"F30.wireOp",EDGE,"E100"),sQuery(id+"F30.wireOp",EDGE,"E101")])]});
            var Q1;
            Q1=qCreatedBy(makeId("Right.planeOp"),FACE);
            mirror(context, id + "F37", {"entities" : qUnion([Q0]), "mirrorPlane" : qUnion([Q1])});
        }
        {
            var Q0;
            Q0=makeQuery(id+"F1.opExtrude","SWEPT_FACE",FACE,{"disambiguationData":[OSD([sQuery(id+"F0.wireOp",EDGE,"E0.bottom")])]});
            var sketch = newSketch(context, id + "F38", { "sketchPlane" : qUnion([Q0])});
            skLineSegment(sketch, "E119", {"start": v(0, 374.52) * mm, "end": v(0, -390.73) * mm, "construction": true});
            skLineSegment(sketch, "E120.0", {"start": v(-880, 374.52) * mm, "end": v(-880, -390.73) * mm, "construction": true});
            skLineSegment(sketch, "E121.0", {"start": v(-925, 374.52) * mm, "end": v(-925, -390.73) * mm, "construction": true});
            skLineSegment(sketch, "E122.0", {"start": v(-874.2, 374.52) * mm, "end": v(-874.2, -390.73) * mm, "construction": true});
            skPoint(sketch, "E123.endSnap0", {"position": v(0, -8.1) * mm});
            skLineSegment(sketch, "E124.0.0", {"start": v(-990, 77.22) * mm, "end": v(-990, -77.22) * mm, "construction": true});
            skLineSegment(sketch, "E124.0.1", {"start": v(-990, -77.22) * mm, "end": v(990, -77.22) * mm, "construction": true});
            skLineSegment(sketch, "E124.0.2", {"start": v(990, -77.22) * mm, "end": v(990, 77.22) * mm, "construction": true});
            skLineSegment(sketch, "E124.0.3", {"start": v(990, 77.22) * mm, "end": v(-990, 77.22) * mm, "construction": true});
            skLineSegment(sketch, "E125", {"start": v(-990, 0) * mm, "end": v(-602.18, 0) * mm, "construction": true});
            skLineSegment(sketch, "E126.0", {"start": v(-990, 60) * mm, "end": v(-602.18, 60) * mm, "construction": true});
            skLineSegment(sketch, "E127.bottom", {"start": v(-925, 60) * mm, "end": v(-874.2, 60) * mm});
            skLineSegment(sketch, "E127.top", {"start": v(-925, -60) * mm, "end": v(-874.2, -60) * mm});
            skLineSegment(sketch, "E127.left", {"start": v(-925, 60) * mm, "end": v(-925, -60) * mm});
            skLineSegment(sketch, "E127.right", {"start": v(-874.2, 60) * mm, "end": v(-874.2, -60) * mm});
            skSolve(sketch);
        }
        {
            var Q0;
            Q0=qSketchRegion(id+"F38",true);
            extrude(context, id + "F39", {"entities" : qUnion([Q0]), "depth" : 120 * mm});
        }
        {
            var Q0;
            Q0=makeQuery(id+"F39.opExtrude","SWEPT_FACE",FACE,{"disambiguationData":[OSD([sQuery(id+"F38.wireOp",EDGE,"E127.left")])]});
            var sketch = newSketch(context, id + "F40", { "sketchPlane" : qUnion([Q0])});
            skLineSegment(sketch, "E128.0", {"start": v(35, -113.53) * mm, "end": v(35, -148.53) * mm, "construction": true});
            skLineSegment(sketch, "E129", {"start": v(35, -131.03) * mm, "end": v(-153.9, -131.03) * mm, "construction": true});
            skLineSegment(sketch, "E130.0", {"start": v(35, 168.97) * mm, "end": v(-153.9, 168.97) * mm, "construction": true});
            skLineSegment(sketch, "E131.0", {"start": v(-60, 201.03) * mm, "end": v(60, 201.03) * mm});
            skLineSegment(sketch, "E132", {"start": v(0, 201.03) * mm, "end": v(0, 143.76) * mm, "construction": true});
            skPoint(sketch, "E132.endSnap0", {"position": v(0, 201.03) * mm});
            skArc(sketch, "E133", {"start": v(-22.5, 168.97) * mm, "mid": v(0, 146.47) * mm, "end": v(22.5, 168.97) * mm});
            skLineSegment(sketch, "E134.0", {"start": v(60, 185.97) * mm, "end": v(22.5, 185.97) * mm});
            skLineSegment(sketch, "E135", {"start": v(-22.5, 168.97) * mm, "end": v(-22.5, 185.97) * mm});
            skLineSegment(sketch, "E136", {"start": v(22.5, 168.97) * mm, "end": v(22.5, 185.97) * mm});
            skLineSegment(sketch, "E137.0", {"start": v(60, 201.03) * mm, "end": v(60, 185.97) * mm});
            skLineSegment(sketch, "E138.0", {"start": v(-60, 201.03) * mm, "end": v(-60, 185.97) * mm});
            skPoint(sketch, "E139.orphan", {"position": v(-60, 81.03) * mm});
            skPoint(sketch, "E140.orphan", {"position": v(60, 81.03) * mm});
            skLineSegment(sketch, "E141.trimOffspring", {"start": v(-22.5, 185.97) * mm, "end": v(-60, 185.97) * mm});
            skSolve(sketch);
        }
        {
            var Q0;
            Q0=qSketchRegion(id+"F40",true);
            extrude(context, id + "F41", {"entities" : qUnion([Q0]), "operationType" : NewBodyOperationType.REMOVE, "endBound" : BoundingType.THROUGH_ALL, "oppositeDirection" : true, "depth" : 25 * mm});
        }
        {
            var Q0;
            Q0=makeQuery(id+"F41.boolean.opBoolean","COPY",FACE,{"derivedFrom":makeQuery(id+"F41.opExtrude","SWEPT_FACE",FACE,{"disambiguationData":[OSD([sQuery(id+"F40.wireOp",EDGE,"E141.trimOffspring")])]})});
            var sketch = newSketch(context, id + "F42", { "sketchPlane" : qUnion([Q0])});
            skLineSegment(sketch, "E142.0", {"start": v(-874.2, 60) * mm, "end": v(-874.2, 22.5) * mm, "construction": true});
            skLineSegment(sketch, "E143.0", {"start": v(-874.2, -60) * mm, "end": v(-925, -60) * mm, "construction": true});
            skLineSegment(sketch, "E144.bottom", {"start": v(-874.2, 60) * mm, "end": v(-880, 60) * mm});
            skLineSegment(sketch, "E144.top", {"start": v(-874.2, -60) * mm, "end": v(-880, -60) * mm});
            skLineSegment(sketch, "E144.left", {"start": v(-874.2, 60) * mm, "end": v(-874.2, -60) * mm});
            skLineSegment(sketch, "E144.right", {"start": v(-880, 60) * mm, "end": v(-880, -60) * mm});
            skLineSegment(sketch, "E145.0", {"start": v(-925, 22.5) * mm, "end": v(-925, 60) * mm, "construction": true});
            skSolve(sketch);
        }
        {
            var Q0;
            Q0=qSketchRegion(id+"F42",true);
            extrude(context, id + "F43", {"entities" : qUnion([Q0]), "operationType" : NewBodyOperationType.REMOVE, "oppositeDirection" : true, "depth" : 92 * mm});
        }
        {
            var Q0;
            Q0=makeQuery(id+"F41.boolean.opBoolean","COPY",FACE,{"derivedFrom":makeQuery(id+"F41.opExtrude","SWEPT_FACE",FACE,{"disambiguationData":[OSD([sQuery(id+"F40.wireOp",EDGE,"E141.trimOffspring")])]})});
            var sketch = newSketch(context, id + "F44", { "sketchPlane" : qUnion([Q0])});
            skLineSegment(sketch, "E146.0.0", {"start": v(-880, 22.5) * mm, "end": v(-880, 60) * mm, "construction": true});
            skLineSegment(sketch, "E146.0.1", {"start": v(-880, 60) * mm, "end": v(-925, 60) * mm, "construction": true});
            skLineSegment(sketch, "E146.0.2", {"start": v(-925, 60) * mm, "end": v(-925, 22.5) * mm, "construction": true});
            skLineSegment(sketch, "E146.0.3", {"start": v(-925, 22.5) * mm, "end": v(-880, 22.5) * mm, "construction": true});
            skLineSegment(sketch, "E147.0.0", {"start": v(-880, -60) * mm, "end": v(-880, -22.5) * mm, "construction": true});
            skLineSegment(sketch, "E147.0.1", {"start": v(-880, -22.5) * mm, "end": v(-925, -22.5) * mm, "construction": true});
            skLineSegment(sketch, "E147.0.2", {"start": v(-925, -22.5) * mm, "end": v(-925, -60) * mm, "construction": true});
            skLineSegment(sketch, "E147.0.3", {"start": v(-925, -60) * mm, "end": v(-880, -60) * mm, "construction": true});
            skLineSegment(sketch, "E148", {"start": v(-902.5, 60) * mm, "end": v(-902.5, -60) * mm, "construction": true});
            skLineSegment(sketch, "E149", {"start": v(-902.5, 0) * mm, "end": v(-937.6, 0) * mm, "construction": true});
            skLineSegment(sketch, "E150.0", {"start": v(-902.5, 37.5) * mm, "end": v(-937.6, 37.5) * mm, "construction": true});
            skPoint(sketch, "E151", {"position": v(-902.5, 37.5) * mm});
            skPoint(sketch, "E152.MirrorP", {"position": v(-902.5, -37.5) * mm});
            skSolve(sketch);
        }
        {
            var Q0;
            Q0=sQuery(id+"F44.wireOp",VERTEX,"E151");
            var Q1;
            Q1=sQuery(id+"F44.wireOp",VERTEX,"E152.MirrorP");
            var Q2;
            Q2=makeQuery(id+"F39.opExtrude","SWEPT_BODY",BODY,{"disambiguationData":[OSD([sQuery(id+"F38.wireOp",EDGE,"E127.bottom"),sQuery(id+"F38.wireOp",EDGE,"E127.top"),sQuery(id+"F38.wireOp",EDGE,"E127.left"),sQuery(id+"F38.wireOp",EDGE,"E127.right")])]});
            hole(context, id + "F45", {"style" : HoleStyle.SIMPLE, "endStyle" : HoleEndStyle.BLIND, "standardTappedOrClearance" : lookupTablePath({ "standard" : "ISO", "engagement" : "75%", "pitch" : "1.25 mm", "size" : "M12", "type" : "Tapped" }), "standardBlindInLast" : lookupTablePath({ "standard" : "ISO", "engagement" : "75%", "pitch" : "1.25 mm", "size" : "M12", "type" : "Tapped" }), "holeDiameter" : 10.8 * mm, "holeDepth" : 35 * mm, "locations" : qUnion([Q0, Q1]), "scope" : qUnion([Q2]), "majorDiameter" : 12 * mm});
        }
        {
            var Q0;
            Q0=makeQuery(id+"F39.opExtrude","SWEPT_BODY",BODY,{"disambiguationData":[OSD([sQuery(id+"F38.wireOp",EDGE,"E127.bottom"),sQuery(id+"F38.wireOp",EDGE,"E127.top"),sQuery(id+"F38.wireOp",EDGE,"E127.left"),sQuery(id+"F38.wireOp",EDGE,"E127.right")])]});
            var Q1;
            Q1=qCreatedBy(makeId("Right.planeOp"),FACE);
            mirror(context, id + "F46", {"entities" : qUnion([Q0]), "mirrorPlane" : qUnion([Q1])});
        }
        {
            var Q0;
            Q0=qCreatedBy(makeId("Right.planeOp"),FACE);
            cPlane(context, id + "F47", {"entities" : qUnion([Q0]), "cplaneType" : CPlaneType.OFFSET, "offset" : (330 / 2 + 15) * mm, "width" : 150 * mm, "height" : 150 * mm});
        }
        {
            var Q0;
            Q0=qCreatedBy(id+"F47.planeOp",FACE);
            var sketch = newSketch(context, id + "F48", { "sketchPlane" : qUnion([Q0])});
            skLineSegment(sketch, "E153", {"start": v(0, 256.72) * mm, "end": v(0, -431.7) * mm, "construction": true});
            skLineSegment(sketch, "E154.0.0", {"start": v(-60, 81.03) * mm, "end": v(-60, 185.97) * mm, "construction": true});
            skLineSegment(sketch, "E154.0.1", {"start": v(-60, 185.97) * mm, "end": v(-22.5, 185.97) * mm, "construction": true});
            skLineSegment(sketch, "E154.0.2", {"start": v(-22.5, 185.97) * mm, "end": v(-22.5, 168.97) * mm, "construction": true});
            skArc(sketch, "E154.0.3", {"start": v(-22.5, 168.97) * mm, "mid": v(0, 146.47) * mm, "end": v(22.5, 168.97) * mm, "construction": true});
            skLineSegment(sketch, "E154.0.4", {"start": v(22.5, 168.97) * mm, "end": v(22.5, 185.97) * mm, "construction": true});
            skLineSegment(sketch, "E154.0.5", {"start": v(22.5, 185.97) * mm, "end": v(144, 185.97) * mm, "construction": true});
            skLineSegment(sketch, "E154.0.6", {"start": v(60, 185.97) * mm, "end": v(60, 81.03) * mm, "construction": true});
            skLineSegment(sketch, "E154.0.7", {"start": v(60, 81.03) * mm, "end": v(-60, 81.03) * mm, "construction": true});
            skLineSegment(sketch, "E155.0", {"start": v(144, 256.72) * mm, "end": v(144, -69.47) * mm});
            skLineSegment(sketch, "E156.0.0", {"start": v(77.22, 81.03) * mm, "end": v(77.22, 69.47) * mm, "construction": true});
            skLineSegment(sketch, "E156.0.1", {"start": v(77.22, 69.47) * mm, "end": v(-77.22, 69.47) * mm, "construction": true});
            skLineSegment(sketch, "E156.0.2", {"start": v(-77.22, 69.47) * mm, "end": v(-77.22, 81.03) * mm, "construction": true});
            skLineSegment(sketch, "E156.0.3", {"start": v(-77.22, 81.03) * mm, "end": v(77.22, 81.03) * mm, "construction": true});
            skLineSegment(sketch, "E157.0.0", {"start": v(-77.22, -69.47) * mm, "end": v(144, -69.47) * mm, "construction": true});
            skLineSegment(sketch, "E157.0.1", {"start": v(77.22, -69.47) * mm, "end": v(77.22, -81.03) * mm, "construction": true});
            skLineSegment(sketch, "E157.0.2", {"start": v(77.22, -81.03) * mm, "end": v(-77.22, -81.03) * mm, "construction": true});
            skLineSegment(sketch, "E157.0.3", {"start": v(-77.22, -81.03) * mm, "end": v(-77.22, -69.47) * mm, "construction": true});
            skLineSegment(sketch, "E158.0.0", {"start": v(16.76, -69.47) * mm, "end": v(-16.76, -69.47) * mm, "construction": true});
            skArc(sketch, "E158.0.1", {"start": v(-16.76, -69.47) * mm, "mid": v(-7.78, -65.75) * mm, "end": v(-4.06, -56.77) * mm, "construction": true});
            skLineSegment(sketch, "E158.0.2", {"start": v(-4.06, -56.77) * mm, "end": v(-4.06, 56.77) * mm, "construction": true});
            skArc(sketch, "E158.0.3", {"start": v(-4.06, 56.77) * mm, "mid": v(-7.78, 65.75) * mm, "end": v(-16.76, 69.47) * mm, "construction": true});
            skLineSegment(sketch, "E158.0.4", {"start": v(-16.76, 69.47) * mm, "end": v(16.76, 69.47) * mm, "construction": true});
            skArc(sketch, "E158.0.5", {"start": v(16.76, 69.47) * mm, "mid": v(7.78, 65.75) * mm, "end": v(4.06, 56.77) * mm, "construction": true});
            skLineSegment(sketch, "E158.0.6", {"start": v(4.06, 56.77) * mm, "end": v(4.06, -56.77) * mm, "construction": true});
            skArc(sketch, "E158.0.7", {"start": v(4.06, -56.77) * mm, "mid": v(7.78, -65.75) * mm, "end": v(16.76, -69.47) * mm, "construction": true});
            skLineSegment(sketch, "E159", {"start": v(144, 185.97) * mm, "end": v(77.22, 197.75) * mm});
            skLineSegment(sketch, "E160.0", {"start": v(70, 86.03) * mm, "end": v(77.22, 86.03) * mm, "construction": true});
            skLineSegment(sketch, "E161.0", {"start": v(77.22, 199.02) * mm, "end": v(77.22, 69.47) * mm});
            skLineSegment(sketch, "E162", {"start": v(144, 30.53) * mm, "end": v(80.74, -69.47) * mm});
            skLineSegment(sketch, "E163", {"start": v(80.74, -69.47) * mm, "end": v(16.76, -69.47) * mm});
            skLineSegment(sketch, "E164", {"start": v(16.76, -69.47) * mm, "end": v(4.06, -56.77) * mm});
            skLineSegment(sketch, "E165", {"start": v(4.06, -56.77) * mm, "end": v(4.06, 56.77) * mm});
            skLineSegment(sketch, "E166", {"start": v(4.06, 56.77) * mm, "end": v(16.76, 69.47) * mm});
            skLineSegment(sketch, "E167", {"start": v(16.76, 69.47) * mm, "end": v(77.22, 69.47) * mm});
            skLineSegment(sketch, "E168", {"start": v(77.22, 69.47) * mm, "end": v(77.22, 86.03) * mm});
            skLineSegment(sketch, "E169", {"start": v(77.22, 86.03) * mm, "end": v(70, 86.03) * mm});
            skLineSegment(sketch, "E170", {"start": v(70, 185.97) * mm, "end": v(70, 199.02) * mm});
            skLineSegment(sketch, "E171", {"start": v(144, 185.97) * mm, "end": v(144, 30.53) * mm});
            skLineSegment(sketch, "E172", {"start": v(77.22, 199.02) * mm, "end": v(91.33, 199.02) * mm});
            skLineSegment(sketch, "E173", {"start": v(77.22, 199.02) * mm, "end": v(150.28, 186.14) * mm});
            skSolve(sketch);
        }
        {
            var Q0;
            Q0=qSketchRegion(id+"F48",true);
            extrude(context, id + "F49", {"entities" : qUnion([Q0]), "oppositeDirection" : true, "depth" : 15.88 * mm});
        }
        {
            var Q0;
            Q0=makeQuery(id+"F49.opExtrude","CAP_FACE",FACE,{"disambiguationData":[OSD([sQuery(id+"F48.wireOp",EDGE,"E159"),sQuery(id+"F48.wireOp",EDGE,"E162"),sQuery(id+"F48.wireOp",EDGE,"E163"),sQuery(id+"F48.wireOp",EDGE,"E164"),sQuery(id+"F48.wireOp",EDGE,"E165"),sQuery(id+"F48.wireOp",EDGE,"E166"),sQuery(id+"F48.wireOp",EDGE,"E167"),sQuery(id+"F48.wireOp",EDGE,"E168"),sQuery(id+"F48.wireOp",EDGE,"E169"),sQuery(id+"F48.wireOp",EDGE,"E170"),sQuery(id+"F48.wireOp",EDGE,"E171")])],"isStart":true});
            var sketch = newSketch(context, id + "F50", { "sketchPlane" : qUnion([Q0])});
            skLineSegment(sketch, "E174.0.4", {"start": v(80.74, -69.47) * mm, "end": v(144, 30.53) * mm});
            skLineSegment(sketch, "E174.0.5", {"start": v(16.76, -69.47) * mm, "end": v(80.74, -69.47) * mm});
            skLineSegment(sketch, "E174.0.6", {"start": v(4.06, -56.77) * mm, "end": v(16.76, -69.47) * mm});
            skLineSegment(sketch, "E174.0.7", {"start": v(4.06, 56.77) * mm, "end": v(4.06, -56.77) * mm});
            skLineSegment(sketch, "E174.0.8", {"start": v(16.76, 69.47) * mm, "end": v(4.06, 56.77) * mm});
            skLineSegment(sketch, "E174.0.9", {"start": v(77.22, 69.47) * mm, "end": v(16.76, 69.47) * mm});
            skLineSegment(sketch, "E174.0.10", {"start": v(77.22, 86.03) * mm, "end": v(77.22, 69.47) * mm});
            skLineSegment(sketch, "E175.0.0", {"start": v(144, 187.25) * mm, "end": v(77.22, 199.02) * mm});
            skLineSegment(sketch, "E175.0.1", {"start": v(77.22, 199.02) * mm, "end": v(77.22, 137.25) * mm});
            skLineSegment(sketch, "E175.0.8", {"start": v(144, 137.25) * mm, "end": v(144, 187.25) * mm});
            skLineSegment(sketch, "E176", {"start": v(77.22, 137.25) * mm, "end": v(144, 137.25) * mm});
            skSolve(sketch);
        }
        {
            var Q0;
            Q0=qSketchRegion(id+"F50",true);
            extrude(context, id + "F51", {"entities" : qUnion([Q0]), "depth" : 19 * mm});
        }
        {
            var Q0;
            Q0=makeQuery(id+"F51.opExtrude","SWEPT_FACE",FACE,{"disambiguationData":[OSD([sQuery(id+"F50.wireOp",EDGE,"E175.0.0")])]});
            var sketch = newSketch(context, id + "F52", { "sketchPlane" : qUnion([Q0])});
            skLineSegment(sketch, "E177", {"start": v(0, 185.79) * mm, "end": v(0, -149.3) * mm, "construction": true});
            skLineSegment(sketch, "E178.0", {"start": v(190, 185.79) * mm, "end": v(190, -149.3) * mm, "construction": true});
            skLineSegment(sketch, "E179.0.0", {"start": v(180, 109.52) * mm, "end": v(180, 34.38) * mm, "construction": true});
            skLineSegment(sketch, "E179.0.1", {"start": v(180, 34.38) * mm, "end": v(205.4, 34.38) * mm, "construction": true});
            skLineSegment(sketch, "E179.0.2", {"start": v(205.4, 34.38) * mm, "end": v(205.4, 109.52) * mm, "construction": true});
            skLineSegment(sketch, "E179.0.3", {"start": v(205.4, 109.52) * mm, "end": v(180, 109.52) * mm, "construction": true});
            skLineSegment(sketch, "E180.0", {"start": v(205.4, 69.52) * mm, "end": v(180, 69.52) * mm, "construction": true});
            skLineSegment(sketch, "E181.0", {"start": v(205.4, 94.52) * mm, "end": v(180, 94.52) * mm, "construction": true});
            skPoint(sketch, "E182", {"position": v(190, 94.52) * mm});
            skPoint(sketch, "E183", {"position": v(190, 69.52) * mm});
            skSolve(sketch);
        }
        {
            var Q0;
            Q0=sQuery(id+"F52.wireOp",VERTEX,"E182");
            var Q1;
            Q1=sQuery(id+"F52.wireOp",VERTEX,"E183");
            var Q2;
            Q2=makeQuery(id+"F51.opExtrude","SWEPT_BODY",BODY,{"disambiguationData":[OSD([sQuery(id+"F50.wireOp",EDGE,"E175.0.0"),sQuery(id+"F50.wireOp",EDGE,"E175.0.1"),sQuery(id+"F50.wireOp",EDGE,"E175.0.8"),sQuery(id+"F50.wireOp",EDGE,"E176")])]});
            hole(context, id + "F53", {"style" : HoleStyle.SIMPLE, "endStyle" : HoleEndStyle.BLIND, "standardTappedOrClearance" : lookupTablePath({ "standard" : "ISO", "engagement" : "75%", "pitch" : "1.5 mm", "size" : "M12", "type" : "Tapped" }), "standardBlindInLast" : lookupTablePath({ "standard" : "ISO", "engagement" : "75%", "pitch" : "1.5 mm", "size" : "M12", "type" : "Tapped" }), "holeDiameter" : 10.5 * mm, "holeDepth" : 30 * mm, "locations" : qUnion([Q0, Q1]), "scope" : qUnion([Q2]), "majorDiameter" : 12 * mm});
        }
        {
            var Q0;
            Q0=makeQuery(id+"F49.opExtrude","SWEPT_BODY",BODY,{"disambiguationData":[OSD([sQuery(id+"F48.wireOp",EDGE,"E159"),sQuery(id+"F48.wireOp",EDGE,"E162"),sQuery(id+"F48.wireOp",EDGE,"E163"),sQuery(id+"F48.wireOp",EDGE,"E164"),sQuery(id+"F48.wireOp",EDGE,"E165"),sQuery(id+"F48.wireOp",EDGE,"E166"),sQuery(id+"F48.wireOp",EDGE,"E167"),sQuery(id+"F48.wireOp",EDGE,"E168"),sQuery(id+"F48.wireOp",EDGE,"E169"),sQuery(id+"F48.wireOp",EDGE,"E170"),sQuery(id+"F48.wireOp",EDGE,"E171")])]});
            var Q1;
            Q1=makeQuery(id+"Fl3NnRKCw4Xixsh_5.opExtrude","SWEPT_BODY",BODY,{"disambiguationData":[OSD([sQuery(id+"F50.wireOp",EDGE,"E174.0.2"),sQuery(id+"F50.wireOp",EDGE,"L5QzTxGx-Pnf6-FATO-cNnD-iBCD0eLFIrfw"),sQuery(id+"F50.wireOp",EDGE,"wuJ0hKJl-j7K5-ufxr-qZVR-Fc0DleJu5Dkg"),sQuery(id+"F50.wireOp",EDGE,"Ftl8TeeW-pfTl-imrB-EIy6-TxBNQzbVambr")])]});
            var Q2;
            Q2=qCreatedBy(makeId("Right.planeOp"),FACE);
            mirror(context, id + "F54", {"entities" : qUnion([Q0, Q1]), "mirrorPlane" : qUnion([Q2])});
        }
        {
            var Q0;
            Q0=qCreatedBy(id+"F47.planeOp",FACE);
            cPlane(context, id + "F55", {"entities" : qUnion([Q0]), "cplaneType" : CPlaneType.OFFSET, "offset" : 350 * mm, "width" : 150 * mm, "height" : 150 * mm});
        }
        {
            var Q0;
            Q0=makeQuery(id+"F49.opExtrude","SWEPT_BODY",BODY,{"disambiguationData":[OSD([sQuery(id+"F48.wireOp",EDGE,"E159"),sQuery(id+"F48.wireOp",EDGE,"E162"),sQuery(id+"F48.wireOp",EDGE,"E163"),sQuery(id+"F48.wireOp",EDGE,"E164"),sQuery(id+"F48.wireOp",EDGE,"E165"),sQuery(id+"F48.wireOp",EDGE,"E166"),sQuery(id+"F48.wireOp",EDGE,"E167"),sQuery(id+"F48.wireOp",EDGE,"E168"),sQuery(id+"F48.wireOp",EDGE,"E169"),sQuery(id+"F48.wireOp",EDGE,"E170"),sQuery(id+"F48.wireOp",EDGE,"E171")])]});
            var Q1;
            Q1=makeQuery(id+"Fl3NnRKCw4Xixsh_5.opExtrude","SWEPT_BODY",BODY,{"disambiguationData":[OSD([sQuery(id+"F50.wireOp",EDGE,"E174.0.2"),sQuery(id+"F50.wireOp",EDGE,"L5QzTxGx-Pnf6-FATO-cNnD-iBCD0eLFIrfw"),sQuery(id+"F50.wireOp",EDGE,"wuJ0hKJl-j7K5-ufxr-qZVR-Fc0DleJu5Dkg"),sQuery(id+"F50.wireOp",EDGE,"Ftl8TeeW-pfTl-imrB-EIy6-TxBNQzbVambr")])]});
            var Q2;
            Q2=qCreatedBy(id+"F55.planeOp",FACE);
            mirror(context, id + "F56", {"entities" : qUnion([Q0, Q1]), "mirrorPlane" : qUnion([Q2])});
        }
        {
            var Q0;
            Q0=makeQuery(id+"F56.opPattern","COPY",BODY,{"derivedFrom":makeQuery(id+"F49.opExtrude","SWEPT_BODY",BODY,{"disambiguationData":[OSD([sQuery(id+"F48.wireOp",EDGE,"E159"),sQuery(id+"F48.wireOp",EDGE,"E162"),sQuery(id+"F48.wireOp",EDGE,"E163"),sQuery(id+"F48.wireOp",EDGE,"E164"),sQuery(id+"F48.wireOp",EDGE,"E165"),sQuery(id+"F48.wireOp",EDGE,"E166"),sQuery(id+"F48.wireOp",EDGE,"E167"),sQuery(id+"F48.wireOp",EDGE,"E168"),sQuery(id+"F48.wireOp",EDGE,"E169"),sQuery(id+"F48.wireOp",EDGE,"E170"),sQuery(id+"F48.wireOp",EDGE,"E171")])]}),"instanceName":"1"});
            var Q1;
            Q1=makeQuery(id+"F56.opPattern","COPY",BODY,{"derivedFrom":makeQuery(id+"Fl3NnRKCw4Xixsh_5.opExtrude","SWEPT_BODY",BODY,{"disambiguationData":[OSD([sQuery(id+"F50.wireOp",EDGE,"E174.0.2"),sQuery(id+"F50.wireOp",EDGE,"L5QzTxGx-Pnf6-FATO-cNnD-iBCD0eLFIrfw"),sQuery(id+"F50.wireOp",EDGE,"wuJ0hKJl-j7K5-ufxr-qZVR-Fc0DleJu5Dkg"),sQuery(id+"F50.wireOp",EDGE,"Ftl8TeeW-pfTl-imrB-EIy6-TxBNQzbVambr")])]}),"instanceName":"1"});
            var Q2;
            Q2=qCreatedBy(makeId("Right.planeOp"),FACE);
            mirror(context, id + "F57", {"entities" : qUnion([Q0, Q1]), "mirrorPlane" : qUnion([Q2])});
        }
        {
            var Q0;
            Q0=qCreatedBy(id+"F47.planeOp",FACE);
            var sketch = newSketch(context, id + "F58", { "sketchPlane" : qUnion([Q0])});
            skLineSegment(sketch, "E184", {"start": v(0, 263.92) * mm, "end": v(0, -250.39) * mm, "construction": true});
            skLineSegment(sketch, "E185.0", {"start": v(-206, 263.92) * mm, "end": v(-206, -250.39) * mm, "construction": true});
            skLineSegment(sketch, "E186.0.0", {"start": v(77.22, 81.03) * mm, "end": v(77.22, 69.47) * mm, "construction": true});
            skLineSegment(sketch, "E186.0.1", {"start": v(77.22, 69.47) * mm, "end": v(-77.22, 69.47) * mm, "construction": true});
            skLineSegment(sketch, "E186.0.2", {"start": v(-77.22, 69.47) * mm, "end": v(-77.22, 81.03) * mm, "construction": true});
            skLineSegment(sketch, "E186.0.3", {"start": v(-77.22, 81.03) * mm, "end": v(77.22, 81.03) * mm, "construction": true});
            skLineSegment(sketch, "E187.0.0", {"start": v(16.76, -69.47) * mm, "end": v(-16.76, -69.47) * mm, "construction": true});
            skArc(sketch, "E187.0.1", {"start": v(-16.76, -69.47) * mm, "mid": v(-7.78, -65.75) * mm, "end": v(-4.06, -56.77) * mm, "construction": true});
            skLineSegment(sketch, "E187.0.2", {"start": v(-4.06, -56.77) * mm, "end": v(-4.06, 56.77) * mm, "construction": true});
            skArc(sketch, "E187.0.3", {"start": v(-4.06, 56.77) * mm, "mid": v(-7.78, 65.75) * mm, "end": v(-16.76, 69.47) * mm, "construction": true});
            skLineSegment(sketch, "E187.0.4", {"start": v(-16.76, 69.47) * mm, "end": v(16.76, 69.47) * mm, "construction": true});
            skArc(sketch, "E187.0.5", {"start": v(16.76, 69.47) * mm, "mid": v(7.78, 65.75) * mm, "end": v(4.06, 56.77) * mm, "construction": true});
            skLineSegment(sketch, "E187.0.6", {"start": v(4.06, 56.77) * mm, "end": v(4.06, -56.77) * mm, "construction": true});
            skArc(sketch, "E187.0.7", {"start": v(4.06, -56.77) * mm, "mid": v(7.78, -65.75) * mm, "end": v(16.76, -69.47) * mm, "construction": true});
            skLineSegment(sketch, "E188.0.0", {"start": v(-77.22, -69.47) * mm, "end": v(77.22, -69.47) * mm, "construction": true});
            skLineSegment(sketch, "E188.0.1", {"start": v(77.22, -69.47) * mm, "end": v(77.22, -81.03) * mm, "construction": true});
            skLineSegment(sketch, "E188.0.2", {"start": v(77.22, -81.03) * mm, "end": v(-77.22, -81.03) * mm, "construction": true});
            skLineSegment(sketch, "E188.0.3", {"start": v(-77.22, -81.03) * mm, "end": v(-77.22, -69.47) * mm, "construction": true});
            skLineSegment(sketch, "E189.0", {"start": v(-206, 10.53) * mm, "end": v(77.22, 10.53) * mm, "construction": true});
            skLineSegment(sketch, "E190", {"start": v(-77.22, 69.47) * mm, "end": v(-16.76, 69.47) * mm});
            skLineSegment(sketch, "E191", {"start": v(-16.76, 69.47) * mm, "end": v(-4.06, 56.77) * mm});
            skLineSegment(sketch, "E192", {"start": v(-4.06, 56.77) * mm, "end": v(-4.06, -56.77) * mm});
            skLineSegment(sketch, "E193", {"start": v(-16.76, -69.47) * mm, "end": v(-4.06, -56.77) * mm});
            skLineSegment(sketch, "E194", {"start": v(-16.76, -69.47) * mm, "end": v(-77.22, -69.47) * mm});
            skLineSegment(sketch, "E195", {"start": v(-77.22, -69.47) * mm, "end": v(-206, 10.53) * mm});
            skLineSegment(sketch, "E196", {"start": v(-77.22, 69.47) * mm, "end": v(-77.22, 185.97) * mm});
            skLineSegment(sketch, "E197.0.0", {"start": v(-60, 81.03) * mm, "end": v(-60, 185.97) * mm});
            skLineSegment(sketch, "E197.0.1", {"start": v(-60, 185.97) * mm, "end": v(-22.5, 185.97) * mm});
            skLineSegment(sketch, "E197.0.2", {"start": v(-22.5, 185.97) * mm, "end": v(-22.5, 168.97) * mm});
            skArc(sketch, "E197.0.3", {"start": v(-22.5, 168.97) * mm, "mid": v(0, 146.47) * mm, "end": v(22.5, 168.97) * mm});
            skLineSegment(sketch, "E197.0.4", {"start": v(22.5, 168.97) * mm, "end": v(22.5, 185.97) * mm});
            skLineSegment(sketch, "E197.0.7", {"start": v(60, 81.03) * mm, "end": v(-60, 81.03) * mm});
            skPoint(sketch, "E197.0.6.start.orphan", {"position": v(60, 185.97) * mm});
            skLineSegment(sketch, "E198", {"start": v(-77.22, 185.97) * mm, "end": v(-222.54, 185.97) * mm, "construction": true});
            skLineSegment(sketch, "E199", {"start": v(-77.22, 185.97) * mm, "end": v(-206, 111.62) * mm});
            skLineSegment(sketch, "E200", {"start": v(-206, 111.62) * mm, "end": v(-206, 10.53) * mm});
            skSolve(sketch);
        }
        {
            var Q0;
            Q0=qSketchRegion(id+"F58",true);
            extrude(context, id + "F59", {"entities" : qUnion([Q0]), "oppositeDirection" : true, "depth" : 16 * mm});
        }
        {
            var Q0;
            Q0=makeQuery(id+"F59.opExtrude","CAP_FACE",FACE,{"disambiguationData":[OSD([sQuery(id+"F58.wireOp",EDGE,"E190"),sQuery(id+"F58.wireOp",EDGE,"E191"),sQuery(id+"F58.wireOp",EDGE,"E192"),sQuery(id+"F58.wireOp",EDGE,"E193"),sQuery(id+"F58.wireOp",EDGE,"E194"),sQuery(id+"F58.wireOp",EDGE,"E195"),sQuery(id+"F58.wireOp",EDGE,"E196"),sQuery(id+"F58.wireOp",EDGE,"E199"),sQuery(id+"F58.wireOp",EDGE,"E200")])],"isStart":false});
            var sketch = newSketch(context, id + "F60", { "sketchPlane" : qUnion([Q0])});
            skLineSegment(sketch, "E201.0.0", {"start": v(206, 111.62) * mm, "end": v(77.22, 185.97) * mm, "construction": true});
            skLineSegment(sketch, "E201.0.1", {"start": v(77.22, 185.97) * mm, "end": v(77.22, 69.47) * mm, "construction": true});
            skLineSegment(sketch, "E201.0.2", {"start": v(77.22, 69.47) * mm, "end": v(16.76, 69.47) * mm, "construction": true});
            skLineSegment(sketch, "E201.0.3", {"start": v(16.76, 69.47) * mm, "end": v(4.06, 56.77) * mm, "construction": true});
            skLineSegment(sketch, "E201.0.4", {"start": v(4.06, 56.77) * mm, "end": v(4.06, -56.77) * mm, "construction": true});
            skLineSegment(sketch, "E201.0.5", {"start": v(4.06, -56.77) * mm, "end": v(16.76, -69.47) * mm, "construction": true});
            skLineSegment(sketch, "E201.0.6", {"start": v(16.76, -69.47) * mm, "end": v(77.22, -69.47) * mm, "construction": true});
            skLineSegment(sketch, "E201.0.7", {"start": v(77.22, -69.47) * mm, "end": v(206, 10.53) * mm, "construction": true});
            skLineSegment(sketch, "E201.0.8", {"start": v(206, 10.53) * mm, "end": v(206, 111.62) * mm, "construction": true});
            skLineSegment(sketch, "E202.0", {"start": v(191, 85.64) * mm, "end": v(62.22, 160) * mm, "construction": true});
            skLineSegment(sketch, "E203", {"start": v(191, 85.64) * mm, "end": v(206, 111.62) * mm, "construction": true});
            skLineSegment(sketch, "E204.0", {"start": v(178, 93.14) * mm, "end": v(193, 119.12) * mm, "construction": true});
            skLineSegment(sketch, "E205.0", {"start": v(100.07, 138.14) * mm, "end": v(115.07, 164.12) * mm, "construction": true});
            skPoint(sketch, "E206", {"position": v(100.07, 138.14) * mm});
            skPoint(sketch, "E207", {"position": v(178, 93.14) * mm});
            skSolve(sketch);
        }
        {
            var Q0;
            Q0=sQuery(id+"F60.wireOp",VERTEX,"E206");
            var Q1;
            Q1=sQuery(id+"F60.wireOp",VERTEX,"E207");
            var Q2;
            Q2=makeQuery(id+"F59.opExtrude","SWEPT_BODY",BODY,{"disambiguationData":[OSD([sQuery(id+"F58.wireOp",EDGE,"E190"),sQuery(id+"F58.wireOp",EDGE,"E191"),sQuery(id+"F58.wireOp",EDGE,"E192"),sQuery(id+"F58.wireOp",EDGE,"E193"),sQuery(id+"F58.wireOp",EDGE,"E194"),sQuery(id+"F58.wireOp",EDGE,"E195"),sQuery(id+"F58.wireOp",EDGE,"E196"),sQuery(id+"F58.wireOp",EDGE,"E199"),sQuery(id+"F58.wireOp",EDGE,"E200")])]});
            hole(context, id + "F61", {"style" : HoleStyle.SIMPLE, "endStyle" : HoleEndStyle.BLIND, "standardTappedOrClearance" : lookupTablePath({ "standard" : "ISO", "size" : "12", "type" : "Drilled" }), "standardBlindInLast" : lookupTablePath({ "standard" : "ISO", "size" : "12", "type" : "Drilled" }), "holeDiameter" : 12 * mm, "holeDepth" : 30 * mm, "locations" : qUnion([Q0, Q1]), "scope" : qUnion([Q2])});
        }
        {
            var Q0;
            Q0=makeQuery(id+"F59.opExtrude","SWEPT_BODY",BODY,{"disambiguationData":[OSD([sQuery(id+"F58.wireOp",EDGE,"E190"),sQuery(id+"F58.wireOp",EDGE,"E191"),sQuery(id+"F58.wireOp",EDGE,"E192"),sQuery(id+"F58.wireOp",EDGE,"E193"),sQuery(id+"F58.wireOp",EDGE,"E194"),sQuery(id+"F58.wireOp",EDGE,"E195"),sQuery(id+"F58.wireOp",EDGE,"E196"),sQuery(id+"F58.wireOp",EDGE,"E199"),sQuery(id+"F58.wireOp",EDGE,"E200")])]});
            var Q1;
            Q1=qCreatedBy(makeId("Right.planeOp"),FACE);
            mirror(context, id + "F62", {"entities" : qUnion([Q0]), "mirrorPlane" : qUnion([Q1])});
        }
        {
            var Q0;
            Q0=makeQuery(id+"F59.opExtrude","SWEPT_BODY",BODY,{"disambiguationData":[OSD([sQuery(id+"F58.wireOp",EDGE,"E190"),sQuery(id+"F58.wireOp",EDGE,"E191"),sQuery(id+"F58.wireOp",EDGE,"E192"),sQuery(id+"F58.wireOp",EDGE,"E193"),sQuery(id+"F58.wireOp",EDGE,"E194"),sQuery(id+"F58.wireOp",EDGE,"E195"),sQuery(id+"F58.wireOp",EDGE,"E196"),sQuery(id+"F58.wireOp",EDGE,"E199"),sQuery(id+"F58.wireOp",EDGE,"E200")])]});
            var Q1;
            Q1=qCreatedBy(id+"F55.planeOp",FACE);
            mirror(context, id + "F63", {"entities" : qUnion([Q0]), "mirrorPlane" : qUnion([Q1])});
        }
        {
            var Q0;
            Q0=makeQuery(id+"F63.opPattern","COPY",BODY,{"derivedFrom":makeQuery(id+"F59.opExtrude","SWEPT_BODY",BODY,{"disambiguationData":[OSD([sQuery(id+"F58.wireOp",EDGE,"E190"),sQuery(id+"F58.wireOp",EDGE,"E191"),sQuery(id+"F58.wireOp",EDGE,"E192"),sQuery(id+"F58.wireOp",EDGE,"E193"),sQuery(id+"F58.wireOp",EDGE,"E194"),sQuery(id+"F58.wireOp",EDGE,"E195"),sQuery(id+"F58.wireOp",EDGE,"E196"),sQuery(id+"F58.wireOp",EDGE,"E199"),sQuery(id+"F58.wireOp",EDGE,"E200")])]}),"instanceName":"1"});
            var Q1;
            Q1=qCreatedBy(makeId("Right.planeOp"),FACE);
            mirror(context, id + "F64", {"operationType" : NewBodyOperationType.ADD, "entities" : qUnion([Q0]), "mirrorPlane" : qUnion([Q1])});
        }
        {
            var Q0;
            Q0=makeQuery(id+"F5.opExtrude","SWEPT_EDGE",EDGE,{"disambiguationData":[OSD([sQuery(id+"F4.wireOp",EDGE,"E50.bottom"),sQuery(id+"F4.wireOp",EDGE,"E50.right")])]});
            var Q1;
            Q1=makeQuery(id+"F5.opExtrude","SWEPT_EDGE",EDGE,{"disambiguationData":[OSD([sQuery(id+"F4.wireOp",EDGE,"E50.top"),sQuery(id+"F4.wireOp",EDGE,"E52.trimOffspring")])]});
            chamfer(context, id + "F65", {"entities" : qUnion([Q0, Q1]), "width" : 5 * mm, "tangentPropagation" : true});
        }
        {
            var Q0;
            Q0=makeQuery(id+"F29.opPattern","COPY",EDGE,{"derivedFrom":makeQuery(id+"F5.opExtrude","SWEPT_EDGE",EDGE,{"disambiguationData":[OSD([sQuery(id+"F4.wireOp",EDGE,"E50.bottom"),sQuery(id+"F4.wireOp",EDGE,"E50.right")])]}),"instanceName":"1"});
            var Q1;
            Q1=makeQuery(id+"F29.opPattern","COPY",EDGE,{"derivedFrom":makeQuery(id+"F5.opExtrude","SWEPT_EDGE",EDGE,{"disambiguationData":[OSD([sQuery(id+"F4.wireOp",EDGE,"E50.top"),sQuery(id+"F4.wireOp",EDGE,"E52.trimOffspring")])]}),"instanceName":"1"});
            chamfer(context, id + "F66", {"entities" : qUnion([Q0, Q1]), "width" : 5 * mm, "tangentPropagation" : true});
        }
        {
            var Q0;
            Q0=makeQuery(id+"F63.opPattern","COPY",FACE,{"derivedFrom":makeQuery(id+"F59.opExtrude","CAP_FACE",FACE,{"disambiguationData":[OSD([sQuery(id+"F58.wireOp",EDGE,"E190"),sQuery(id+"F58.wireOp",EDGE,"E191"),sQuery(id+"F58.wireOp",EDGE,"E192"),sQuery(id+"F58.wireOp",EDGE,"E193"),sQuery(id+"F58.wireOp",EDGE,"E194"),sQuery(id+"F58.wireOp",EDGE,"E195"),sQuery(id+"F58.wireOp",EDGE,"E196"),sQuery(id+"F58.wireOp",EDGE,"E199"),sQuery(id+"F58.wireOp",EDGE,"E200")])],"isStart":false}),"instanceName":"1"});
            var sketch = newSketch(context, id + "F67", { "sketchPlane" : qUnion([Q0])});
            skLineSegment(sketch, "E208.0", {"start": v(-35, -113.53) * mm, "end": v(-35, -148.53) * mm, "construction": true});
            skLineSegment(sketch, "E209", {"start": v(-35, -131.03) * mm, "end": v(-367.6, -131.03) * mm, "construction": true});
            skLineSegment(sketch, "E210.0", {"start": v(-35, -16.03) * mm, "end": v(-367.6, -16.03) * mm, "construction": true});
            skLineSegment(sketch, "E211.0", {"start": v(-35, 23.97) * mm, "end": v(-367.6, 23.97) * mm, "construction": true});
            skLineSegment(sketch, "E212", {"start": v(0, 332.63) * mm, "end": v(0, -263.23) * mm, "construction": true});
            skLineSegment(sketch, "E213.0", {"start": v(-140, 23.97) * mm, "end": v(-140, -16.03) * mm, "construction": true});
            skLineSegment(sketch, "E214.trimOffspring", {"start": v(-140, -131.03) * mm, "end": v(-140, -263.23) * mm, "construction": true});
            skLineSegment(sketch, "E215.bottom", {"start": v(-160, 23.97) * mm, "end": v(-120, 23.97) * mm});
            skLineSegment(sketch, "E215.top", {"start": v(-160, -16.03) * mm, "end": v(-120, -16.03) * mm});
            skLineSegment(sketch, "E215.left", {"start": v(-160, 23.97) * mm, "end": v(-160, -16.03) * mm});
            skLineSegment(sketch, "E215.right", {"start": v(-120, 23.97) * mm, "end": v(-120, -16.03) * mm});
            skPoint(sketch, "E215.middle", {"position": v(-140, 3.97) * mm});
            skSolve(sketch);
        }
        {
            var Q0;
            Q0=qSketchRegion(id+"F67",true);
            extrude(context, id + "F68", {"entities" : qUnion([Q0]), "depth" : 60 * mm});
        }
        {
            var Q0;
            Q0=makeQuery(id+"F68.opExtrude","SWEPT_FACE",FACE,{"disambiguationData":[OSD([sQuery(id+"F67.wireOp",EDGE,"E215.bottom")])]});
            var sketch = newSketch(context, id + "F69", { "sketchPlane" : qUnion([Q0])});
            skLineSegment(sketch, "E216.0", {"start": v(917.5, -35) * mm, "end": v(952.5, -35) * mm, "construction": true});
            skLineSegment(sketch, "E217", {"start": v(935, -120) * mm, "end": v(935, -160) * mm, "construction": true});
            skLineSegment(sketch, "E218.0.0", {"start": v(896, -120) * mm, "end": v(896, -160) * mm, "construction": true});
            skLineSegment(sketch, "E218.0.1", {"start": v(896, -160) * mm, "end": v(956, -160) * mm, "construction": true});
            skLineSegment(sketch, "E218.0.2", {"start": v(956, -160) * mm, "end": v(956, -120) * mm, "construction": true});
            skLineSegment(sketch, "E218.0.3", {"start": v(956, -120) * mm, "end": v(896, -120) * mm, "construction": true});
            skLineSegment(sketch, "E219", {"start": v(956, -140) * mm, "end": v(857.2, -140) * mm, "construction": true});
            skPoint(sketch, "E219.endSnap0", {"position": v(956, -140) * mm});
            skPoint(sketch, "E220.orphan", {"position": v(935, -35) * mm});
            skPoint(sketch, "E221", {"position": v(935, -140) * mm});
            skSolve(sketch);
        }
        {
            var Q0;
            Q0=sQuery(id+"F69.wireOp",VERTEX,"E221");
            var Q1;
            Q1=makeQuery(id+"F68.opExtrude","SWEPT_BODY",BODY,{"disambiguationData":[OSD([sQuery(id+"F67.wireOp",EDGE,"E215.bottom"),sQuery(id+"F67.wireOp",EDGE,"E215.top"),sQuery(id+"F67.wireOp",EDGE,"E215.left"),sQuery(id+"F67.wireOp",EDGE,"E215.right")])]});
            hole(context, id + "F70", {"style" : HoleStyle.SIMPLE, "endStyle" : HoleEndStyle.THROUGH, "standardTappedOrClearance" : lookupTablePath({ "standard" : "ISO", "size" : "20", "type" : "Drilled" }), "standardBlindInLast" : lookupTablePath({ "standard" : "ISO", "size" : "20", "type" : "Drilled" }), "holeDiameter" : 20 * mm, "locations" : qUnion([Q0]), "scope" : qUnion([Q1]), "isTappedThrough" : true});
        }
        {
            var Q0;
            Q0=makeQuery(id+"F68.opExtrude","SWEPT_FACE",FACE,{"disambiguationData":[OSD([sQuery(id+"F67.wireOp",EDGE,"E215.left")])]});
            var sketch = newSketch(context, id + "F71", { "sketchPlane" : qUnion([Q0])});
            skLineSegment(sketch, "E222.0", {"start": v(925, 23.97) * mm, "end": v(945, 23.97) * mm, "construction": true});
            skLineSegment(sketch, "E223", {"start": v(935, 23.97) * mm, "end": v(935, -16.03) * mm, "construction": true});
            skLineSegment(sketch, "E224.0", {"start": v(956, -16.03) * mm, "end": v(896, -16.03) * mm, "construction": true});
            skPoint(sketch, "E225", {"position": v(935, 3.97) * mm});
            skSolve(sketch);
        }
        {
            var Q0;
            Q0=sQuery(id+"F71.wireOp",VERTEX,"E225");
            var Q1;
            Q1=makeQuery(id+"F68.opExtrude","SWEPT_BODY",BODY,{"disambiguationData":[OSD([sQuery(id+"F67.wireOp",EDGE,"E215.bottom"),sQuery(id+"F67.wireOp",EDGE,"E215.top"),sQuery(id+"F67.wireOp",EDGE,"E215.left"),sQuery(id+"F67.wireOp",EDGE,"E215.right")])]});
            hole(context, id + "F72", {"style" : HoleStyle.SIMPLE, "endStyle" : HoleEndStyle.THROUGH, "standardTappedOrClearance" : lookupTablePath({ "standard" : "ISO", "size" : "8", "type" : "Drilled" }), "standardBlindInLast" : lookupTablePath({ "standard" : "ISO", "size" : "8", "type" : "Drilled" }), "holeDiameter" : 8 * mm, "locations" : qUnion([Q0]), "scope" : qUnion([Q1]), "isTappedThrough" : true});
        }
        {
            var Q0;
            Q0=makeQuery(id+"F68.opExtrude","SWEPT_BODY",BODY,{"disambiguationData":[OSD([sQuery(id+"F67.wireOp",EDGE,"E215.bottom"),sQuery(id+"F67.wireOp",EDGE,"E215.top"),sQuery(id+"F67.wireOp",EDGE,"E215.left"),sQuery(id+"F67.wireOp",EDGE,"E215.right")])]});
            var Q1;
            Q1=qCreatedBy(makeId("Right.planeOp"),FACE);
            mirror(context, id + "F73", {"entities" : qUnion([Q0]), "mirrorPlane" : qUnion([Q1])});
        }
        {
            var Q0;
            Q0=makeQuery(id+"F51.opExtrude","SWEPT_BODY",BODY,{"disambiguationData":[OSD([sQuery(id+"F50.wireOp",EDGE,"E175.0.0"),sQuery(id+"F50.wireOp",EDGE,"E175.0.1"),sQuery(id+"F50.wireOp",EDGE,"E175.0.8"),sQuery(id+"F50.wireOp",EDGE,"E176")])]});
            var Q1;
            Q1=qCreatedBy(id+"F55.planeOp",FACE);
            mirror(context, id + "F74", {"entities" : qUnion([Q0]), "mirrorPlane" : qUnion([Q1])});
        }
        {
            var Q0;
            Q0=makeQuery(id+"F51.opExtrude","SWEPT_BODY",BODY,{"disambiguationData":[OSD([sQuery(id+"F50.wireOp",EDGE,"E175.0.0"),sQuery(id+"F50.wireOp",EDGE,"E175.0.1"),sQuery(id+"F50.wireOp",EDGE,"E175.0.8"),sQuery(id+"F50.wireOp",EDGE,"E176")])]});
            var Q1;
            Q1=makeQuery(id+"F74.opPattern","COPY",BODY,{"derivedFrom":makeQuery(id+"F51.opExtrude","SWEPT_BODY",BODY,{"disambiguationData":[OSD([sQuery(id+"F50.wireOp",EDGE,"E175.0.0"),sQuery(id+"F50.wireOp",EDGE,"E175.0.1"),sQuery(id+"F50.wireOp",EDGE,"E175.0.8"),sQuery(id+"F50.wireOp",EDGE,"E176")])]}),"instanceName":"1"});
            var Q2;
            Q2=qCreatedBy(makeId("Right.planeOp"),FACE);
            mirror(context, id + "F75", {"entities" : qUnion([Q0, Q1]), "mirrorPlane" : qUnion([Q2])});
        }
        {
            var Q0;
            Q0=makeQuery(id+"F1.opExtrude","SWEPT_BODY",BODY,{"disambiguationData":[OSD([sQuery(id+"F0.wireOp",EDGE,"E0.bottom"),sQuery(id+"F0.wireOp",EDGE,"E0.top"),sQuery(id+"F0.wireOp",EDGE,"E0.left"),sQuery(id+"F0.wireOp",EDGE,"E0.right"),sQuery(id+"F0.wireOp",EDGE,"E2.0"),sQuery(id+"F0.wireOp",EDGE,"E3.0"),sQuery(id+"F0.wireOp",EDGE,"E4.0"),sQuery(id+"F0.wireOp",EDGE,"E5.0"),sQuery(id+"F0.wireOp",EDGE,"E6.trimOffspring"),sQuery(id+"F0.wireOp",EDGE,"E7.trimOffspring"),sQuery(id+"F0.wireOp",EDGE,"E8.trimOffspring"),sQuery(id+"F0.wireOp",EDGE,"E9.trimOffspring"),sQuery(id+"F0.wireOp",EDGE,"E10.filletArc"),sQuery(id+"F0.wireOp",EDGE,"E11.filletArc"),sQuery(id+"F0.wireOp",EDGE,"E12.filletArc"),sQuery(id+"F0.wireOp",EDGE,"E13.filletArc")])]});
            var Q1;
            Q1=makeQuery(id+"F62.opPattern","COPY",BODY,{"derivedFrom":makeQuery(id+"F59.opExtrude","SWEPT_BODY",BODY,{"disambiguationData":[OSD([sQuery(id+"F58.wireOp",EDGE,"E190"),sQuery(id+"F58.wireOp",EDGE,"E191"),sQuery(id+"F58.wireOp",EDGE,"E192"),sQuery(id+"F58.wireOp",EDGE,"E193"),sQuery(id+"F58.wireOp",EDGE,"E194"),sQuery(id+"F58.wireOp",EDGE,"E195"),sQuery(id+"F58.wireOp",EDGE,"E196"),sQuery(id+"F58.wireOp",EDGE,"E199"),sQuery(id+"F58.wireOp",EDGE,"E200")])]}),"instanceName":"1"});
            var Q2;
            Q2=makeQuery(id+"F59.opExtrude","SWEPT_BODY",BODY,{"disambiguationData":[OSD([sQuery(id+"F58.wireOp",EDGE,"E190"),sQuery(id+"F58.wireOp",EDGE,"E191"),sQuery(id+"F58.wireOp",EDGE,"E192"),sQuery(id+"F58.wireOp",EDGE,"E193"),sQuery(id+"F58.wireOp",EDGE,"E194"),sQuery(id+"F58.wireOp",EDGE,"E195"),sQuery(id+"F58.wireOp",EDGE,"E196"),sQuery(id+"F58.wireOp",EDGE,"E199"),sQuery(id+"F58.wireOp",EDGE,"E200")])]});
            booleanBodies(context, id + "F76", {"operationType" : BooleanOperationType.UNION, "tools" : qUnion([Q0, Q1, Q2])});
        }
        {
            var Q0;
            Q0=makeQuery(id+"F1.opExtrude","SWEPT_FACE",FACE,{"disambiguationData":[OSD([sQuery(id+"F0.wireOp",EDGE,"E8.trimOffspring")])]});
            var sketch = newSketch(context, id + "F77", { "sketchPlane" : qUnion([Q0])});
            skLineSegment(sketch, "E226.0", {"start": v(990, -81.03) * mm, "end": v(-990, -81.03) * mm, "construction": true});
            skLineSegment(sketch, "E227", {"start": v(0, 255.13) * mm, "end": v(0, -180.02) * mm, "construction": true});
            skLineSegment(sketch, "E228.0", {"start": v(990, 18.97) * mm, "end": v(-990, 18.97) * mm, "construction": true});
            skLineSegment(sketch, "E229.0", {"start": v(1002.25, -56.03) * mm, "end": v(-990, -56.03) * mm, "construction": true});
            skArc(sketch, "E230", {"start": v(81.12, -56.03) * mm, "mid": v(6.12, 18.97) * mm, "end": v(-68.88, -56.03) * mm});
            skLineSegment(sketch, "E231", {"start": v(-68.88, -56.03) * mm, "end": v(-68.87, -81.03) * mm});
            skLineSegment(sketch, "E232", {"start": v(81.12, -56.03) * mm, "end": v(81.12, -81.03) * mm});
            skLineSegment(sketch, "E233.0", {"start": v(-80, -56.03) * mm, "end": v(-80, -81.03) * mm});
            skArc(sketch, "E233.1", {"start": v(92.25, -56.03) * mm, "mid": v(6.13, 30.1) * mm, "end": v(-80, -56.03) * mm});
            skLineSegment(sketch, "E233.2", {"start": v(92.25, -56.03) * mm, "end": v(92.25, -81.03) * mm});
            skLineSegment(sketch, "E234", {"start": v(-80, -81.03) * mm, "end": v(-68.87, -81.03) * mm});
            skLineSegment(sketch, "E235", {"start": v(81.12, -81.03) * mm, "end": v(92.25, -81.03) * mm});
            skSolve(sketch);
        }
        {
            var Q0;
            Q0=qSketchRegion(id+"F77",true);
            var Q1;
            Q1=makeQuery(id+"F1.opExtrude","SWEPT_FACE",FACE,{"disambiguationData":[OSD([sQuery(id+"F0.wireOp",EDGE,"E9.trimOffspring")])]});
            extrude(context, id + "F78", {"entities" : qUnion([Q0]), "operationType" : NewBodyOperationType.ADD, "endBound" : BoundingType.UP_TO_SURFACE, "oppositeDirection" : true, "endBoundEntityFace" : qUnion([Q1]), "depth" : 25 * mm});
        }
        {
            var Q0;
            Q0=makeQuery(id+"F78.boolean.opBoolean","MERGE",FACE,{"derivedFrom":[makeQuery(id+"F1.opExtrude","SWEPT_FACE",FACE,{"disambiguationData":[OSD([sQuery(id+"F0.wireOp",EDGE,"E8.trimOffspring")])]}),makeQuery(id+"F78.opExtrude","CAP_FACE",FACE,{"disambiguationData":[OSD([sQuery(id+"F77.wireOp",EDGE,"E230"),sQuery(id+"F77.wireOp",EDGE,"E231"),sQuery(id+"F77.wireOp",EDGE,"E232"),sQuery(id+"F77.wireOp",EDGE,"E233.0"),sQuery(id+"F77.wireOp",EDGE,"E233.1"),sQuery(id+"F77.wireOp",EDGE,"E233.2"),sQuery(id+"F77.wireOp",EDGE,"E234"),sQuery(id+"F77.wireOp",EDGE,"E235")])],"isStart":true})]});
            var sketch = newSketch(context, id + "F79", { "sketchPlane" : qUnion([Q0])});
            skArc(sketch, "E236.0", {"start": v(81.12, -56.03) * mm, "mid": v(6.12, 18.97) * mm, "end": v(-68.88, -56.03) * mm});
            skLineSegment(sketch, "E237.0", {"start": v(-68.88, -56.03) * mm, "end": v(-68.87, -81.03) * mm});
            skLineSegment(sketch, "E238.0", {"start": v(81.12, -56.03) * mm, "end": v(81.12, -81.03) * mm});
            skLineSegment(sketch, "E239.0", {"start": v(81.12, -81.03) * mm, "end": v(-68.88, -81.03) * mm});
            skPoint(sketch, "E240.orphan", {"position": v(81.12, -69.47) * mm});
            skPoint(sketch, "E241.orphan", {"position": v(-68.87, -69.47) * mm});
            skPoint(sketch, "E242.orphan", {"position": v(990, -81.03) * mm});
            skPoint(sketch, "E243.orphan", {"position": v(-990, -81.03) * mm});
            skSolve(sketch);
        }
        {
            var Q0;
            Q0=qSketchRegion(id+"F79",true);
            var Q1;
            {var subQ0=sQuery(id+"F0.wireOp",EDGE,"E9.trimOffspring");Q1=makeQuery(id+"F78.boolean.opBoolean","MERGE",FACE,{"derivedFrom":[makeQuery(id+"F1.opExtrude","SWEPT_FACE",FACE,{"disambiguationData":[OSD([subQ0])]}),makeQuery(id+"F78.opExtrude","CAP_FACE",FACE,{"disambiguationData":[OSD([subQ0])],"isStart":false})]});}
            extrude(context, id + "F80", {"entities" : qUnion([Q0]), "operationType" : NewBodyOperationType.REMOVE, "endBound" : BoundingType.UP_TO_SURFACE, "oppositeDirection" : true, "endBoundEntityFace" : qUnion([Q1]), "depth" : 25 * mm});
        }
        {
            var Q0;
            Q0=makeQuery(id+"F78.boolean.opBoolean","MERGE",FACE,{"derivedFrom":[makeQuery(id+"F1.opExtrude","SWEPT_FACE",FACE,{"disambiguationData":[OSD([sQuery(id+"F0.wireOp",EDGE,"E8.trimOffspring")])]}),makeQuery(id+"F78.opExtrude","CAP_FACE",FACE,{"disambiguationData":[OSD([sQuery(id+"F77.wireOp",EDGE,"E230"),sQuery(id+"F77.wireOp",EDGE,"E231"),sQuery(id+"F77.wireOp",EDGE,"E232"),sQuery(id+"F77.wireOp",EDGE,"E233.0"),sQuery(id+"F77.wireOp",EDGE,"E233.1"),sQuery(id+"F77.wireOp",EDGE,"E233.2"),sQuery(id+"F77.wireOp",EDGE,"E234"),sQuery(id+"F77.wireOp",EDGE,"E235")])],"isStart":true})]});
            var sketch = newSketch(context, id + "F81", { "sketchPlane" : qUnion([Q0])});
            skArc(sketch, "E244.0", {"start": v(81.12, -56.03) * mm, "mid": v(6.12, 18.97) * mm, "end": v(-68.88, -56.03) * mm});
            skLineSegment(sketch, "E245.0", {"start": v(-68.88, -56.03) * mm, "end": v(-68.87, -81.03) * mm});
            skLineSegment(sketch, "E246.0", {"start": v(81.12, -56.03) * mm, "end": v(81.12, -81.03) * mm});
            skLineSegment(sketch, "E247.0", {"start": v(-94.28, -56.03) * mm, "end": v(-94.27, -81.03) * mm});
            skArc(sketch, "E247.1", {"start": v(106.52, -56.03) * mm, "mid": v(6.13, 44.37) * mm, "end": v(-94.28, -56.03) * mm});
            skLineSegment(sketch, "E247.2", {"start": v(106.52, -56.03) * mm, "end": v(106.52, -81.03) * mm});
            skLineSegment(sketch, "E248", {"start": v(-94.27, -81.03) * mm, "end": v(-68.87, -81.03) * mm});
            skLineSegment(sketch, "E249", {"start": v(81.12, -81.03) * mm, "end": v(106.52, -81.03) * mm});
            skSolve(sketch);
        }
        {
            var Q0;
            Q0 = qSketchRegion(id + "F81", true);
            var Q1;
            {var subQ0=sQuery(id+"F0.wireOp",EDGE,"E9.trimOffspring");Q1=makeQuery(id+"F78.boolean.opBoolean","MERGE",FACE,{"derivedFrom":[makeQuery(id+"F1.opExtrude","SWEPT_FACE",FACE,{"disambiguationData":[OSD([subQ0])]}),makeQuery(id+"F78.opExtrude","CAP_FACE",FACE,{"disambiguationData":[OSD([subQ0])],"isStart":false})]});}
            var Q2;
            Q2=makeQuery(id+"F1.opExtrude","SWEPT_BODY",BODY,{"disambiguationData":[OSD([sQuery(id+"F0.wireOp",EDGE,"E0.bottom"),sQuery(id+"F0.wireOp",EDGE,"E0.top"),sQuery(id+"F0.wireOp",EDGE,"E0.left"),sQuery(id+"F0.wireOp",EDGE,"E0.right"),sQuery(id+"F0.wireOp",EDGE,"E2.0"),sQuery(id+"F0.wireOp",EDGE,"E3.0"),sQuery(id+"F0.wireOp",EDGE,"E4.0"),sQuery(id+"F0.wireOp",EDGE,"E5.0"),sQuery(id+"F0.wireOp",EDGE,"E6.trimOffspring"),sQuery(id+"F0.wireOp",EDGE,"E7.trimOffspring"),sQuery(id+"F0.wireOp",EDGE,"E8.trimOffspring"),sQuery(id+"F0.wireOp",EDGE,"E9.trimOffspring"),sQuery(id+"F0.wireOp",EDGE,"E10.filletArc"),sQuery(id+"F0.wireOp",EDGE,"E11.filletArc"),sQuery(id+"F0.wireOp",EDGE,"E12.filletArc"),sQuery(id+"F0.wireOp",EDGE,"E13.filletArc")])]});
            extrude(context, id + "F82", {"entities" : qUnion([Q0]), "operationType" : NewBodyOperationType.ADD, "endBound" : BoundingType.UP_TO_SURFACE, "oppositeDirection" : true, "endBoundEntityFace" : qUnion([Q1]), "endBoundEntityBody" : qUnion([Q2]), "depth" : 25 * mm});
        }
        {
            var Q0;
            Q0=makeQuery(id+"F82.boolean.opBoolean","MERGE",FACE,{"derivedFrom":[makeQuery(id+"F78.boolean.opBoolean","MERGE",FACE,{"derivedFrom":[makeQuery(id+"F1.opExtrude","SWEPT_FACE",FACE,{"disambiguationData":[OSD([sQuery(id+"F0.wireOp",EDGE,"E8.trimOffspring")])]}),makeQuery(id+"F78.opExtrude","CAP_FACE",FACE,{"disambiguationData":[OSD([sQuery(id+"F77.wireOp",EDGE,"E230"),sQuery(id+"F77.wireOp",EDGE,"E231"),sQuery(id+"F77.wireOp",EDGE,"E232"),sQuery(id+"F77.wireOp",EDGE,"E233.0"),sQuery(id+"F77.wireOp",EDGE,"E233.1"),sQuery(id+"F77.wireOp",EDGE,"E233.2"),sQuery(id+"F77.wireOp",EDGE,"E234"),sQuery(id+"F77.wireOp",EDGE,"E235")])],"isStart":true})]}),makeQuery(id+"F82.opExtrude","CAP_FACE",FACE,{"disambiguationData":[OSD([sQuery(id+"F81.wireOp",EDGE,"E244.0"),sQuery(id+"F81.wireOp",EDGE,"E245.0"),sQuery(id+"F81.wireOp",EDGE,"E246.0"),sQuery(id+"F81.wireOp",EDGE,"E247.0"),sQuery(id+"F81.wireOp",EDGE,"E247.1"),sQuery(id+"F81.wireOp",EDGE,"E247.2"),sQuery(id+"F81.wireOp",EDGE,"E248"),sQuery(id+"F81.wireOp",EDGE,"E249")])],"isStart":true})]});
            cPlane(context, id + "F83", {"entities" : qUnion([Q0]), "cplaneType" : CPlaneType.OFFSET, "offset" : 12.5 * mm, "oppositeDirection" : true, "width" : 150 * mm, "height" : 150 * mm});
        }
        {
            var Q0;
            Q0=qCreatedBy(id+"F83.planeOp",FACE);
            var sketch = newSketch(context, id + "F84", { "sketchPlane" : qUnion([Q0])});
            skLineSegment(sketch, "E250.0", {"start": v(164, 69.47) * mm, "end": v(-164, 69.47) * mm});
            skLineSegment(sketch, "E251.0.0", {"start": v(-164, 185.97) * mm, "end": v(-164, 111.62) * mm});
            skLineSegment(sketch, "E251.0.1", {"start": v(-164, 111.62) * mm, "end": v(-164, 10.53) * mm});
            skLineSegment(sketch, "E251.0.2", {"start": v(-164, 10.53) * mm, "end": v(-164, -69.47) * mm});
            skLineSegment(sketch, "E251.0.4", {"start": v(-164, -69.47) * mm, "end": v(-164, -56.77) * mm});
            skLineSegment(sketch, "E251.0.5", {"start": v(-164, -56.77) * mm, "end": v(-164, 56.77) * mm});
            skLineSegment(sketch, "E251.0.6", {"start": v(-164, 56.77) * mm, "end": v(-164, 69.47) * mm});
            skLineSegment(sketch, "E251.0.8", {"start": v(-164, 69.47) * mm, "end": v(-164, 81.03) * mm});
            skLineSegment(sketch, "E251.0.9", {"start": v(-164, 81.03) * mm, "end": v(-164, 185.97) * mm});
            skLineSegment(sketch, "E252.0", {"start": v(-94.27, -69.47) * mm, "end": v(-164, -69.47) * mm});
            skArc(sketch, "E253.0", {"start": v(106.52, -56.03) * mm, "mid": v(6.13, 44.37) * mm, "end": v(-94.28, -56.03) * mm});
            skPoint(sketch, "E254.0", {"position": v(-94.28, -62.75) * mm});
            skLineSegment(sketch, "E255.0", {"start": v(106.52, -56.03) * mm, "end": v(106.52, -69.47) * mm});
            skLineSegment(sketch, "E256.0", {"start": v(164, -69.47) * mm, "end": v(106.52, -69.47) * mm});
            skLineSegment(sketch, "E257.0.0", {"start": v(164, 111.62) * mm, "end": v(164, 185.97) * mm});
            skLineSegment(sketch, "E257.0.1", {"start": v(164, 185.97) * mm, "end": v(164, 81.03) * mm});
            skLineSegment(sketch, "E257.0.2", {"start": v(164, 81.03) * mm, "end": v(164, 69.47) * mm});
            skLineSegment(sketch, "E257.0.4", {"start": v(164, 69.47) * mm, "end": v(164, 56.77) * mm});
            skLineSegment(sketch, "E257.0.5", {"start": v(164, 56.77) * mm, "end": v(164, -56.77) * mm});
            skLineSegment(sketch, "E257.0.6", {"start": v(164, -56.77) * mm, "end": v(164, -69.47) * mm});
            skLineSegment(sketch, "E257.0.8", {"start": v(164, -69.47) * mm, "end": v(164, 10.53) * mm});
            skLineSegment(sketch, "E257.0.9", {"start": v(164, 10.53) * mm, "end": v(164, 111.62) * mm});
            skLineSegment(sketch, "E258.0", {"start": v(-94.28, -56.03) * mm, "end": v(-94.27, -69.47) * mm});
            skSolve(sketch);
        }
        {
            var Q0;
            Q0 = qSketchRegion(id + "F84", true);
            extrude(context, id + "F85", {"entities" : qUnion([Q0]), "oppositeDirection" : true, "depth" : (25) * mm});
        }
        {
            var Q0;
            Q0=makeQuery(id+"F85.opExtrude","SWEPT_BODY",BODY,{"disambiguationData":[OSD([sQuery(id+"F84.wireOp",EDGE,"E250.0"),sQuery(id+"F84.wireOp",EDGE,"E251.0.4"),sQuery(id+"F84.wireOp",EDGE,"E251.0.5"),sQuery(id+"F84.wireOp",EDGE,"E251.0.6"),sQuery(id+"F84.wireOp",EDGE,"E252.0"),sQuery(id+"F84.wireOp",EDGE,"E253.0"),sQuery(id+"F84.wireOp",EDGE,"E255.0"),sQuery(id+"F84.wireOp",EDGE,"E256.0"),sQuery(id+"F84.wireOp",EDGE,"E257.0.8"),sQuery(id+"F84.wireOp",EDGE,"E257.0.9"),sQuery(id+"F84.wireOp",EDGE,"E258.0")])]});
            var Q1;
            Q1=qCreatedBy(makeId("Front.planeOp"),FACE);
            mirror(context, id + "F86", {"operationType" : NewBodyOperationType.ADD, "entities" : qUnion([Q0]), "mirrorPlane" : qUnion([Q1])});
        }
        {
            var Q0;
            Q0=makeQuery(id+"F82.boolean.opBoolean","MERGE",FACE,{"derivedFrom":[makeQuery(id+"F78.boolean.opBoolean","MERGE",FACE,{"derivedFrom":[makeQuery(id+"F1.opExtrude","SWEPT_FACE",FACE,{"disambiguationData":[OSD([sQuery(id+"F0.wireOp",EDGE,"E8.trimOffspring")])]}),makeQuery(id+"F78.opExtrude","CAP_FACE",FACE,{"disambiguationData":[OSD([sQuery(id+"F77.wireOp",EDGE,"E230"),sQuery(id+"F77.wireOp",EDGE,"E231"),sQuery(id+"F77.wireOp",EDGE,"E232"),sQuery(id+"F77.wireOp",EDGE,"E233.0"),sQuery(id+"F77.wireOp",EDGE,"E233.1"),sQuery(id+"F77.wireOp",EDGE,"E233.2"),sQuery(id+"F77.wireOp",EDGE,"E234"),sQuery(id+"F77.wireOp",EDGE,"E235")])],"isStart":true})]}),makeQuery(id+"F82.opExtrude","CAP_FACE",FACE,{"disambiguationData":[OSD([sQuery(id+"F81.wireOp",EDGE,"E244.0"),sQuery(id+"F81.wireOp",EDGE,"E245.0"),sQuery(id+"F81.wireOp",EDGE,"E246.0"),sQuery(id+"F81.wireOp",EDGE,"E247.0"),sQuery(id+"F81.wireOp",EDGE,"E247.1"),sQuery(id+"F81.wireOp",EDGE,"E247.2"),sQuery(id+"F81.wireOp",EDGE,"E248"),sQuery(id+"F81.wireOp",EDGE,"E249")])],"isStart":true})]});
            var sketch = newSketch(context, id + "F87", { "sketchPlane" : qUnion([Q0])});
            skLineSegment(sketch, "E259.0", {"start": v(109.44, -69.47) * mm, "end": v(0, -69.47) * mm, "construction": true});
            skPoint(sketch, "E260.orphan", {"position": v(-94.27, -69.47) * mm});
            skLineSegment(sketch, "E261.0", {"start": v(-68.87, -69.47) * mm, "end": v(-68.87, -81.03) * mm, "construction": true});
            skPoint(sketch, "E262.orphan", {"position": v(-164, -69.47) * mm});
            skLineSegment(sketch, "E263.trimOffspring", {"start": v(-68.88, -69.47) * mm, "end": v(-94.27, -69.47) * mm, "construction": true});
            skPoint(sketch, "E264.orphan", {"position": v(-68.88, -56.03) * mm});
            skLineSegment(sketch, "E265.bottom", {"start": v(-68.87, -81.03) * mm, "end": v(-81.57, -81.03) * mm});
            skLineSegment(sketch, "E265.top", {"start": v(-68.87, -69.47) * mm, "end": v(-81.57, -69.47) * mm});
            skLineSegment(sketch, "E265.left", {"start": v(-68.87, -81.03) * mm, "end": v(-68.87, -69.47) * mm});
            skLineSegment(sketch, "E265.right", {"start": v(-81.57, -81.03) * mm, "end": v(-81.57, -69.47) * mm});
            skArc(sketch, "E266.0", {"start": v(81.12, -56.03) * mm, "mid": v(6.12, 18.97) * mm, "end": v(-68.88, -56.03) * mm, "construction": true});
            skLineSegment(sketch, "E267", {"start": v(6.12, -56.03) * mm, "end": v(6.12, -22.88) * mm, "construction": true});
            skLineSegment(sketch, "E268.MirrorCS", {"start": v(81.12, -69.47) * mm, "end": v(93.82, -69.47) * mm});
            skLineSegment(sketch, "E269.MirrorCS", {"start": v(81.12, -81.03) * mm, "end": v(81.12, -69.47) * mm});
            skLineSegment(sketch, "E270.MirrorCS", {"start": v(81.12, -69.47) * mm, "end": v(81.12, -81.03) * mm, "construction": true});
            skPoint(sketch, "E271.MirrorP", {"position": v(106.52, -69.47) * mm});
            skPoint(sketch, "E272.MirrorP", {"position": v(81.12, -56.03) * mm});
            skLineSegment(sketch, "E273.MirrorCS", {"start": v(81.12, -81.03) * mm, "end": v(93.82, -81.03) * mm});
            skLineSegment(sketch, "E274.MirrorCS", {"start": v(81.12, -69.47) * mm, "end": v(106.52, -69.47) * mm, "construction": true});
            skLineSegment(sketch, "E275.MirrorCS", {"start": v(93.82, -81.03) * mm, "end": v(93.82, -69.47) * mm});
            skSolve(sketch);
        }
        {
            var Q0;
            Q0 = qSketchRegion(id + "F87", true);
            extrude(context, id + "F88", {"entities" : qUnion([Q0]), "operationType" : NewBodyOperationType.REMOVE, "endBound" : BoundingType.THROUGH_ALL, "oppositeDirection" : true, "depth" : 25 * mm});
        }
    });
